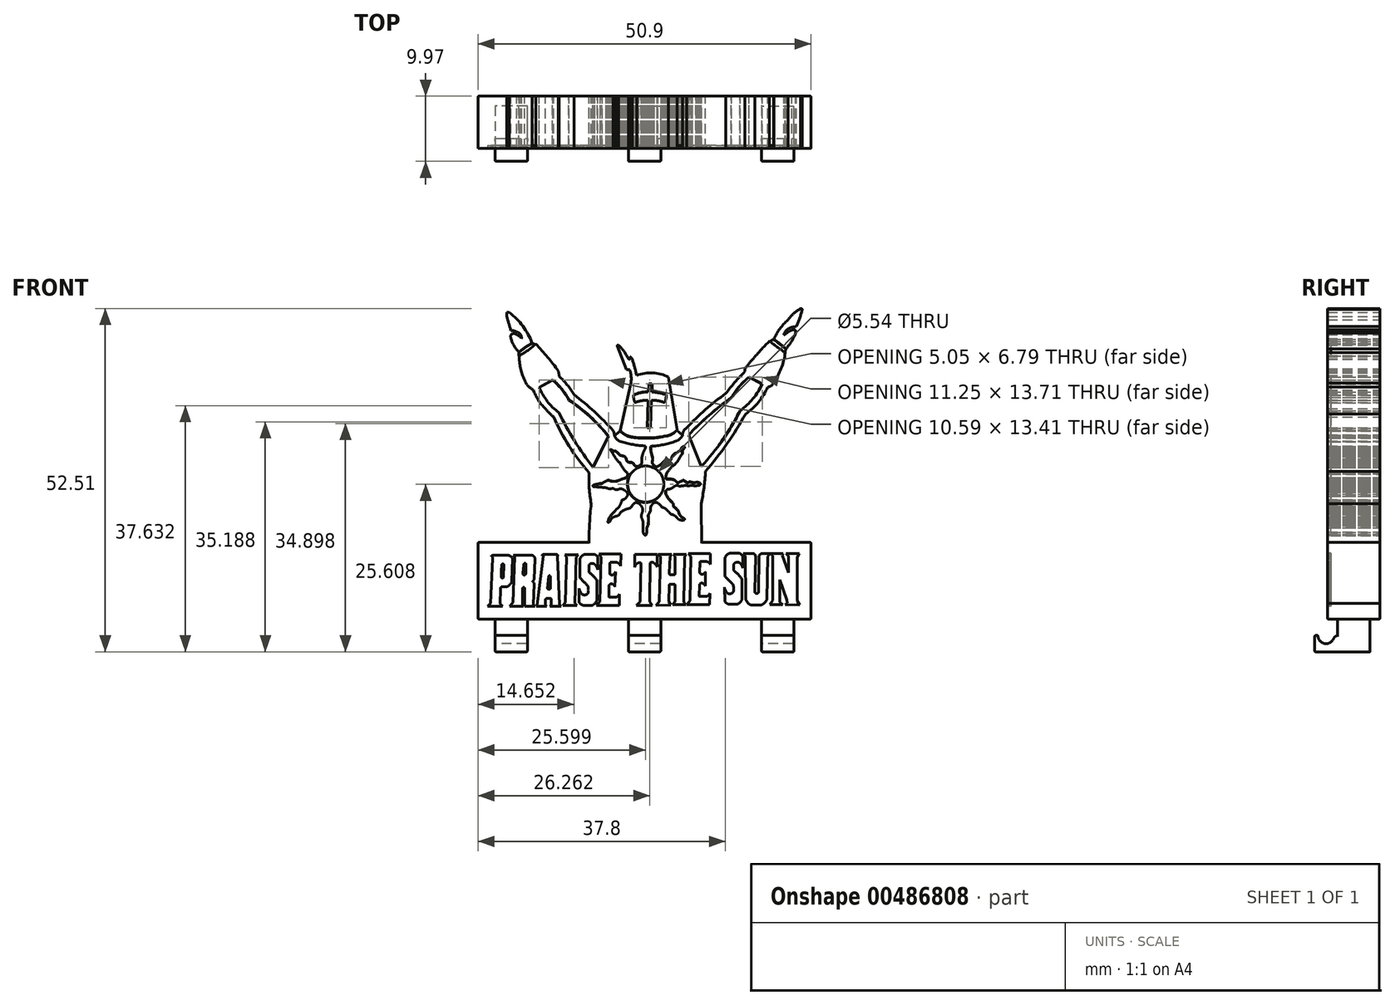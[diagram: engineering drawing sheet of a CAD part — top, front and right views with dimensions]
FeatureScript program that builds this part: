
annotation { "Feature Type Name" : "Feature", "Feature Type Description" : "" }
export const myFeature = defineFeature(function(context is Context, id is Id, definition is map)
    precondition{}
    {
        {
            var Q0;
            Q0=qCreatedBy(makeId("Front.planeOp"),FACE);
            var sketch = newSketch(context, id + "F0", { "sketchPlane" : qUnion([Q0])});
            skArc(sketch, "E0", {"start": v(-17.35, 21.56) * mm, "mid": v(-18.77, 24.15) * mm, "end": v(-20.84, 26.27) * mm});
            skLineSegment(sketch, "E1", {"start": v(-20.84, 26.27) * mm, "end": v(-21.25, 26.27) * mm});
            skLineSegment(sketch, "E2", {"start": v(-21.25, 26.27) * mm, "end": v(-21.25, 25.65) * mm});
            skArc(sketch, "E3", {"start": v(-21.25, 25.65) * mm, "mid": v(-20.93, 24.57) * mm, "end": v(-20.6, 23.5) * mm});
            skArc(sketch, "E4", {"start": v(-19.13, 22.87) * mm, "mid": v(-19.8, 23.33) * mm, "end": v(-20.6, 23.5) * mm});
            skArc(sketch, "E5", {"start": v(-18.99, 22.28) * mm, "mid": v(-19, 22.59) * mm, "end": v(-19.13, 22.87) * mm});
            skArc(sketch, "E6", {"start": v(-18.99, 22.28) * mm, "mid": v(-19.33, 22.61) * mm, "end": v(-19.74, 22.87) * mm});
            skArc(sketch, "E7", {"start": v(-19.74, 22.87) * mm, "mid": v(-20.17, 23.01) * mm, "end": v(-20.6, 22.87) * mm});
            skArc(sketch, "E8", {"start": v(-20.6, 22.87) * mm, "mid": v(-20.64, 22.57) * mm, "end": v(-20.6, 22.28) * mm});
            skArc(sketch, "E9", {"start": v(-20.6, 22.28) * mm, "mid": v(-20.1, 21.15) * mm, "end": v(-19.34, 20.18) * mm});
            skLineSegment(sketch, "E10", {"start": v(-17.35, 21.56) * mm, "end": v(-16.8, 21.42) * mm});
            skLineSegment(sketch, "E11", {"start": v(-19.34, 20.18) * mm, "end": v(-19.34, 19.66) * mm});
            skArc(sketch, "E12", {"start": v(-19.34, 19.66) * mm, "mid": v(-19.14, 17.75) * mm, "end": v(-18.52, 15.93) * mm});
            skArc(sketch, "E13", {"start": v(-18.52, 15.93) * mm, "mid": v(-18, 15.05) * mm, "end": v(-17.18, 14.43) * mm});
            skArc(sketch, "E14", {"start": v(-13.38, 17.3) * mm, "mid": v(-15, 19.43) * mm, "end": v(-16.8, 21.42) * mm});
            skArc(sketch, "E15", {"start": v(-13.25, 16.5) * mm, "mid": v(-13.28, 16.9) * mm, "end": v(-13.38, 17.3) * mm});
            skArc(sketch, "E16", {"start": v(-17.18, 14.43) * mm, "mid": v(-16.44, 12.88) * mm, "end": v(-15.37, 11.55) * mm});
            skArc(sketch, "E17", {"start": v(-10.97, 13.68) * mm, "mid": v(-12, 15.18) * mm, "end": v(-13.25, 16.5) * mm});
            skArc(sketch, "E18", {"start": v(-15.37, 11.55) * mm, "mid": v(-14.74, 10.88) * mm, "end": v(-14.07, 10.25) * mm});
            skArc(sketch, "E19", {"start": v(-14.07, 10.25) * mm, "mid": v(-11.7, 5.8) * mm, "end": v(-8.67, 1.79) * mm});
            skArc(sketch, "E20", {"start": v(-4.98, 8.2) * mm, "mid": v(-7.86, 11.08) * mm, "end": v(-10.97, 13.68) * mm});
            skArc(sketch, "E21", {"start": v(-4.77, 7.4) * mm, "mid": v(-4.84, 7.81) * mm, "end": v(-4.98, 8.2) * mm});
            skArc(sketch, "E22", {"start": v(-4.77, 7.4) * mm, "mid": v(-4.4, 6.86) * mm, "end": v(-3.88, 6.5) * mm});
            skArc(sketch, "E23", {"start": v(-3.88, 6.5) * mm, "mid": v(-1.96, 6.06) * mm, "end": v(0, 5.82) * mm});
            skArc(sketch, "E24", {"start": v(-8.67, 1.79) * mm, "mid": v(-8.64, -0.62) * mm, "end": v(-8.33, -3) * mm});
            skArc(sketch, "E25", {"start": v(-8.33, -3) * mm, "mid": v(-8.58, -5.96) * mm, "end": v(-8.67, -8.91) * mm});
            skLineSegment(sketch, "E26", {"start": v(-8.67, -8.91) * mm, "end": v(-24.71, -8.91) * mm});
            skLineSegment(sketch, "E27", {"start": v(-19.4, -10.71) * mm, "end": v(-19.4, -8.91) * mm, "construction": true});
            skLineSegment(sketch, "E28", {"start": v(-25.63, -18.85) * mm, "end": v(-25.63, -8.91) * mm});
            skLineSegment(sketch, "E29", {"start": v(-25.63, -8.91) * mm, "end": v(-24.71, -8.91) * mm});
            skLineSegment(sketch, "E30", {"start": v(-25.63, -18.85) * mm, "end": v(-25.63, -20.65) * mm, "construction": true});
            skLineSegment(sketch, "E31", {"start": v(-25.63, -20.65) * mm, "end": v(25.27, -20.65) * mm});
            skLineSegment(sketch, "E32", {"start": v(23.64, -18.26) * mm, "end": v(25.24, -18.26) * mm, "construction": true});
            skLineSegment(sketch, "E33", {"start": v(8.52, -8.91) * mm, "end": v(25.24, -8.91) * mm});
            skLineSegment(sketch, "E34", {"start": v(25.24, -8.91) * mm, "end": v(25.24, -18.26) * mm});
            skArc(sketch, "E35", {"start": v(8.52, -8.91) * mm, "mid": v(8.5, -5.96) * mm, "end": v(8.46, -3.01) * mm});
            skArc(sketch, "E36", {"start": v(8.46, -3.01) * mm, "mid": v(8.9, -0.54) * mm, "end": v(9.12, 1.96) * mm});
            skArc(sketch, "E37", {"start": v(9.12, 1.96) * mm, "mid": v(12.42, 6.18) * mm, "end": v(15.24, 10.73) * mm});
            skArc(sketch, "E38", {"start": v(15.24, 10.73) * mm, "mid": v(17.24, 12.54) * mm, "end": v(18.63, 14.86) * mm});
            skArc(sketch, "E39", {"start": v(18.63, 14.86) * mm, "mid": v(19.16, 15.03) * mm, "end": v(19.48, 15.48) * mm});
            skArc(sketch, "E40", {"start": v(19.48, 15.48) * mm, "mid": v(20.68, 17.68) * mm, "end": v(21.32, 20.1) * mm});
            skArc(sketch, "E41", {"start": v(21.42, 20.7) * mm, "mid": v(22.27, 21.81) * mm, "end": v(22.87, 23.07) * mm});
            skLineSegment(sketch, "E42", {"start": v(21.42, 20.7) * mm, "end": v(21.32, 20.1) * mm});
            skArc(sketch, "E43", {"start": v(22.87, 23.07) * mm, "mid": v(22.92, 23.31) * mm, "end": v(22.87, 23.55) * mm});
            skArc(sketch, "E44", {"start": v(22.87, 23.55) * mm, "mid": v(22.6, 23.61) * mm, "end": v(22.33, 23.55) * mm});
            skArc(sketch, "E45", {"start": v(22.33, 23.55) * mm, "mid": v(21.74, 23.26) * mm, "end": v(21.24, 22.84) * mm});
            skArc(sketch, "E46", {"start": v(21.11, 22.92) * mm, "mid": v(21.16, 22.85) * mm, "end": v(21.24, 22.84) * mm});
            skArc(sketch, "E47", {"start": v(22.16, 23.94) * mm, "mid": v(21.51, 23.56) * mm, "end": v(21.11, 22.92) * mm});
            skArc(sketch, "E48", {"start": v(23, 24.1) * mm, "mid": v(22.58, 24.04) * mm, "end": v(22.16, 23.94) * mm});
            skArc(sketch, "E49", {"start": v(23, 24.1) * mm, "mid": v(23.53, 25.38) * mm, "end": v(23.9, 26.72) * mm});
            skArc(sketch, "E50", {"start": v(23.9, 26.72) * mm, "mid": v(23.8, 26.84) * mm, "end": v(23.64, 26.85) * mm});
            skArc(sketch, "E51", {"start": v(23.64, 26.85) * mm, "mid": v(22.6, 26.08) * mm, "end": v(21.74, 25.12) * mm});
            skArc(sketch, "E52", {"start": v(21.74, 25.12) * mm, "mid": v(20.5, 23.76) * mm, "end": v(19.57, 22.17) * mm});
            skArc(sketch, "E53", {"start": v(18.92, 21.86) * mm, "mid": v(17.77, 20.71) * mm, "end": v(16.7, 19.49) * mm});
            skLineSegment(sketch, "E54", {"start": v(18.92, 21.86) * mm, "end": v(19.57, 22.17) * mm});
            skArc(sketch, "E55", {"start": v(16.7, 19.49) * mm, "mid": v(15.9, 18.58) * mm, "end": v(15.17, 17.62) * mm});
            skArc(sketch, "E56", {"start": v(15.17, 17.62) * mm, "mid": v(15.12, 17.42) * mm, "end": v(15.17, 17.22) * mm});
            skArc(sketch, "E57", {"start": v(15.17, 17.22) * mm, "mid": v(13.64, 15.6) * mm, "end": v(12.24, 13.86) * mm});
            skArc(sketch, "E58", {"start": v(12.24, 13.86) * mm, "mid": v(9.11, 11.38) * mm, "end": v(6.25, 8.6) * mm});
            skArc(sketch, "E59", {"start": v(6.25, 8.6) * mm, "mid": v(5.8, 8.15) * mm, "end": v(5.64, 7.54) * mm});
            skArc(sketch, "E60", {"start": v(4.62, 6.59) * mm, "mid": v(5.24, 6.95) * mm, "end": v(5.64, 7.54) * mm});
            skArc(sketch, "E61", {"start": v(0.76, 5.77) * mm, "mid": v(2.72, 6.04) * mm, "end": v(4.62, 6.59) * mm});
            skLineSegment(sketch, "E62", {"start": v(-4.77, 7.4) * mm, "end": v(-3.88, 8.17) * mm});
            skLineSegment(sketch, "E63", {"start": v(5.64, 7.54) * mm, "end": v(4.77, 8.3) * mm});
            skLineSegment(sketch, "E64", {"start": v(-3.88, 8.17) * mm, "end": v(-2.3, 15.25) * mm});
            skArc(sketch, "E65", {"start": v(-2.3, 15.25) * mm, "mid": v(-2.22, 16.4) * mm, "end": v(-2.47, 17.52) * mm});
            skLineSegment(sketch, "E66", {"start": v(-2.47, 17.52) * mm, "end": v(-2.97, 17.52) * mm});
            skLineSegment(sketch, "E67", {"start": v(-2.97, 17.52) * mm, "end": v(-4.36, 21.12) * mm});
            skArc(sketch, "E68", {"start": v(-4.31, 21.26) * mm, "mid": v(-4.36, 21.2) * mm, "end": v(-4.36, 21.12) * mm});
            skArc(sketch, "E69", {"start": v(-4.18, 21.26) * mm, "mid": v(-4.24, 21.28) * mm, "end": v(-4.31, 21.26) * mm});
            skArc(sketch, "E70", {"start": v(-2.66, 19.18) * mm, "mid": v(-3.32, 20.28) * mm, "end": v(-4.18, 21.26) * mm});
            skArc(sketch, "E71", {"start": v(-2.66, 19.18) * mm, "mid": v(-2.52, 19.11) * mm, "end": v(-2.39, 19.18) * mm});
            skArc(sketch, "E72", {"start": v(-2.39, 19.5) * mm, "mid": v(-2.41, 19.33) * mm, "end": v(-2.39, 19.18) * mm});
            skArc(sketch, "E73", {"start": v(-2.07, 19.13) * mm, "mid": v(-2.2, 19.33) * mm, "end": v(-2.39, 19.5) * mm});
            skArc(sketch, "E74", {"start": v(-1.4, 16.64) * mm, "mid": v(-1.7, 17.89) * mm, "end": v(-2.07, 19.13) * mm});
            skArc(sketch, "E75", {"start": v(3.5, 16.39) * mm, "mid": v(1.07, 17) * mm, "end": v(-1.4, 16.64) * mm});
            skLineSegment(sketch, "E76", {"start": v(3.5, 16.39) * mm, "end": v(4.77, 8.3) * mm});
            skCircle(sketch, "E77", {"center": v(0, 0) * mm, "radius": 2.77 * mm});
            skArc(sketch, "E78", {"start": v(-1.42, 2.69) * mm, "mid": v(-0.96, 2.83) * mm, "end": v(-0.6, 3.15) * mm});
            skArc(sketch, "E79", {"start": v(-1.84, 3.1) * mm, "mid": v(-1.66, 2.86) * mm, "end": v(-1.42, 2.69) * mm});
            skArc(sketch, "E80", {"start": v(-1.84, 3.1) * mm, "mid": v(-2.08, 3.3) * mm, "end": v(-2.4, 3.35) * mm});
            skArc(sketch, "E81", {"start": v(-2.94, 3.73) * mm, "mid": v(-2.73, 3.45) * mm, "end": v(-2.4, 3.35) * mm});
            skArc(sketch, "E82", {"start": v(-2.94, 3.73) * mm, "mid": v(-3, 3.96) * mm, "end": v(-3.13, 4.16) * mm});
            skArc(sketch, "E83", {"start": v(-3.13, 4.16) * mm, "mid": v(-3.47, 4.33) * mm, "end": v(-3.84, 4.4) * mm});
            skArc(sketch, "E84", {"start": v(-3.84, 4.4) * mm, "mid": v(-4.2, 4.71) * mm, "end": v(-4.54, 5.03) * mm});
            skArc(sketch, "E85", {"start": v(-4.54, 5.03) * mm, "mid": v(-4.74, 5.09) * mm, "end": v(-4.93, 5.03) * mm});
            skArc(sketch, "E86", {"start": v(-4.93, 5.03) * mm, "mid": v(-5.1, 5.2) * mm, "end": v(-5.34, 5.29) * mm});
            skArc(sketch, "E87", {"start": v(-5.34, 5.29) * mm, "mid": v(-5.39, 5.3) * mm, "end": v(-5.43, 5.27) * mm});
            skArc(sketch, "E88", {"start": v(-4.87, 4.36) * mm, "mid": v(-5.13, 4.83) * mm, "end": v(-5.43, 5.27) * mm});
            skArc(sketch, "E89", {"start": v(-4.87, 4.36) * mm, "mid": v(-4.4, 3.72) * mm, "end": v(-3.86, 3.14) * mm});
            skArc(sketch, "E90", {"start": v(-3.86, 3.14) * mm, "mid": v(-3.4, 2.35) * mm, "end": v(-2.79, 1.68) * mm});
            skArc(sketch, "E91", {"start": v(-2.97, 1) * mm, "mid": v(-2.8, 1.32) * mm, "end": v(-2.79, 1.68) * mm});
            skArc(sketch, "E92", {"start": v(-2.97, 1) * mm, "mid": v(-3.66, 0.78) * mm, "end": v(-4.33, 0.5) * mm});
            skArc(sketch, "E93", {"start": v(-5.33, 0.5) * mm, "mid": v(-4.83, 0.44) * mm, "end": v(-4.33, 0.5) * mm});
            skArc(sketch, "E94", {"start": v(-5.33, 0.5) * mm, "mid": v(-5.7, 0.6) * mm, "end": v(-6.05, 0.5) * mm});
            skArc(sketch, "E95", {"start": v(-6.05, 0.5) * mm, "mid": v(-6.37, 0.32) * mm, "end": v(-6.65, 0.12) * mm});
            skArc(sketch, "E96", {"start": v(-6.65, 0.12) * mm, "mid": v(-7.01, 0.1) * mm, "end": v(-7.36, 0) * mm});
            skArc(sketch, "E97", {"start": v(-7.36, 0) * mm, "mid": v(-7.57, 0) * mm, "end": v(-7.75, -0.1) * mm});
            skArc(sketch, "E98", {"start": v(-7.75, -0.1) * mm, "mid": v(-7.9, -0.11) * mm, "end": v(-8.04, -0.18) * mm});
            skArc(sketch, "E99", {"start": v(-8.04, -0.18) * mm, "mid": v(-8.06, -0.31) * mm, "end": v(-7.96, -0.4) * mm});
            skArc(sketch, "E100", {"start": v(-7.96, -0.4) * mm, "mid": v(-7.45, -0.43) * mm, "end": v(-6.93, -0.45) * mm});
            skArc(sketch, "E101", {"start": v(-6.93, -0.45) * mm, "mid": v(-6.45, -0.52) * mm, "end": v(-5.96, -0.57) * mm});
            skArc(sketch, "E102", {"start": v(-5.96, -0.57) * mm, "mid": v(-5.6, -0.71) * mm, "end": v(-5.2, -0.68) * mm});
            skArc(sketch, "E103", {"start": v(-4.92, -0.68) * mm, "mid": v(-5.06, -0.63) * mm, "end": v(-5.2, -0.68) * mm});
            skArc(sketch, "E104", {"start": v(-4.92, -0.68) * mm, "mid": v(-4.58, -0.86) * mm, "end": v(-4.2, -0.83) * mm});
            skArc(sketch, "E105", {"start": v(-3.54, -0.77) * mm, "mid": v(-3.88, -0.7) * mm, "end": v(-4.2, -0.83) * mm});
            skArc(sketch, "E106", {"start": v(-2.85, -1.23) * mm, "mid": v(-3.18, -0.98) * mm, "end": v(-3.54, -0.77) * mm});
            skArc(sketch, "E107", {"start": v(-2.85, -1.84) * mm, "mid": v(-2.74, -1.53) * mm, "end": v(-2.85, -1.23) * mm});
            skArc(sketch, "E108", {"start": v(-3.5, -2.4) * mm, "mid": v(-3.12, -2.18) * mm, "end": v(-2.85, -1.84) * mm});
            skArc(sketch, "E109", {"start": v(-3.5, -2.4) * mm, "mid": v(-3.65, -2.46) * mm, "end": v(-3.67, -2.62) * mm});
            skArc(sketch, "E110", {"start": v(-4.14, -3.6) * mm, "mid": v(-3.89, -3.12) * mm, "end": v(-3.67, -2.62) * mm});
            skArc(sketch, "E111", {"start": v(-4.14, -3.6) * mm, "mid": v(-4.5, -3.86) * mm, "end": v(-4.75, -4.2) * mm});
            skArc(sketch, "E112", {"start": v(-4.75, -4.2) * mm, "mid": v(-5.43, -4.91) * mm, "end": v(-5.81, -5.82) * mm});
            skArc(sketch, "E113", {"start": v(-5.81, -5.82) * mm, "mid": v(-5.63, -5.83) * mm, "end": v(-5.48, -5.72) * mm});
            skArc(sketch, "E114", {"start": v(-4.75, -4.96) * mm, "mid": v(-5.2, -5.26) * mm, "end": v(-5.48, -5.72) * mm});
            skArc(sketch, "E115", {"start": v(-4.75, -4.96) * mm, "mid": v(-4.37, -4.86) * mm, "end": v(-4.03, -4.67) * mm});
            skArc(sketch, "E116", {"start": v(-3.35, -3.99) * mm, "mid": v(-3.75, -4.27) * mm, "end": v(-4.03, -4.67) * mm});
            skArc(sketch, "E117", {"start": v(-2.4, -3.67) * mm, "mid": v(-2.88, -3.81) * mm, "end": v(-3.35, -3.99) * mm});
            skArc(sketch, "E118", {"start": v(-2.4, -3.67) * mm, "mid": v(-2.28, -3.6) * mm, "end": v(-2.21, -3.5) * mm});
            skArc(sketch, "E119", {"start": v(-1.6, -2.84) * mm, "mid": v(-1.95, -3.13) * mm, "end": v(-2.21, -3.5) * mm});
            skArc(sketch, "E120", {"start": v(-1.08, -2.94) * mm, "mid": v(-1.33, -2.85) * mm, "end": v(-1.6, -2.84) * mm});
            skArc(sketch, "E121", {"start": v(-0.53, -3.6) * mm, "mid": v(-0.77, -3.24) * mm, "end": v(-1.08, -2.94) * mm});
            skArc(sketch, "E122", {"start": v(-0.58, -4.46) * mm, "mid": v(-0.49, -4.03) * mm, "end": v(-0.53, -3.6) * mm});
            skArc(sketch, "E123", {"start": v(-0.58, -4.46) * mm, "mid": v(-0.67, -4.8) * mm, "end": v(-0.64, -5.16) * mm});
            skArc(sketch, "E124", {"start": v(-0.39, -5.95) * mm, "mid": v(-0.48, -5.54) * mm, "end": v(-0.64, -5.16) * mm});
            skArc(sketch, "E125", {"start": v(-0.39, -7.32) * mm, "mid": v(-0.38, -6.63) * mm, "end": v(-0.39, -5.95) * mm});
            skArc(sketch, "E126", {"start": v(-0.39, -7.32) * mm, "mid": v(-0.31, -7.6) * mm, "end": v(-0.12, -7.82) * mm});
            skArc(sketch, "E127", {"start": v(-0.12, -7.82) * mm, "mid": v(0.02, -7.78) * mm, "end": v(0.1, -7.65) * mm});
            skArc(sketch, "E128", {"start": v(0.1, -7.65) * mm, "mid": v(0.18, -7.16) * mm, "end": v(0.19, -6.66) * mm});
            skArc(sketch, "E129", {"start": v(0.19, -6.66) * mm, "mid": v(0.26, -6.52) * mm, "end": v(0.28, -6.36) * mm});
            skArc(sketch, "E130", {"start": v(0.28, -6.36) * mm, "mid": v(0.37, -6.26) * mm, "end": v(0.4, -6.12) * mm});
            skArc(sketch, "E131", {"start": v(0.4, -6.12) * mm, "mid": v(0.42, -5.4) * mm, "end": v(0.4, -4.67) * mm});
            skArc(sketch, "E132", {"start": v(0.4, -4.67) * mm, "mid": v(0.49, -4.58) * mm, "end": v(0.54, -4.46) * mm});
            skArc(sketch, "E133", {"start": v(0.54, -4.46) * mm, "mid": v(0.62, -4.34) * mm, "end": v(0.65, -4.2) * mm});
            skArc(sketch, "E134", {"start": v(0.65, -4.2) * mm, "mid": v(0.75, -4.03) * mm, "end": v(0.75, -3.83) * mm});
            skArc(sketch, "E135", {"start": v(0.85, -3.32) * mm, "mid": v(0.76, -3.57) * mm, "end": v(0.75, -3.83) * mm});
            skArc(sketch, "E136", {"start": v(1.3, -2.84) * mm, "mid": v(1.04, -3.05) * mm, "end": v(0.85, -3.32) * mm});
            skArc(sketch, "E137", {"start": v(1.86, -2.9) * mm, "mid": v(1.58, -2.82) * mm, "end": v(1.3, -2.84) * mm});
            skArc(sketch, "E138", {"start": v(2.39, -3.42) * mm, "mid": v(2.15, -3.13) * mm, "end": v(1.86, -2.9) * mm});
            skArc(sketch, "E139", {"start": v(2.39, -3.42) * mm, "mid": v(2.5, -3.56) * mm, "end": v(2.69, -3.6) * mm});
            skArc(sketch, "E140", {"start": v(3.4, -4.14) * mm, "mid": v(3.08, -3.82) * mm, "end": v(2.69, -3.6) * mm});
            skArc(sketch, "E141", {"start": v(3.92, -4.67) * mm, "mid": v(3.66, -4.4) * mm, "end": v(3.4, -4.14) * mm});
            skArc(sketch, "E142", {"start": v(3.92, -4.67) * mm, "mid": v(4.03, -4.68) * mm, "end": v(4.14, -4.67) * mm});
            skArc(sketch, "E143", {"start": v(4.81, -5.21) * mm, "mid": v(4.51, -4.9) * mm, "end": v(4.14, -4.67) * mm});
            skArc(sketch, "E144", {"start": v(4.81, -5.21) * mm, "mid": v(5.02, -5.38) * mm, "end": v(5.26, -5.48) * mm});
            skArc(sketch, "E145", {"start": v(5.26, -5.48) * mm, "mid": v(5.6, -5.52) * mm, "end": v(5.94, -5.48) * mm});
            skArc(sketch, "E146", {"start": v(5.94, -5.48) * mm, "mid": v(5.93, -5.32) * mm, "end": v(5.8, -5.21) * mm});
            skArc(sketch, "E147", {"start": v(5.12, -4.53) * mm, "mid": v(5.41, -4.92) * mm, "end": v(5.8, -5.21) * mm});
            skArc(sketch, "E148", {"start": v(5.04, -4.2) * mm, "mid": v(5.08, -4.37) * mm, "end": v(5.12, -4.53) * mm});
            skArc(sketch, "E149", {"start": v(5.04, -4.2) * mm, "mid": v(4.7, -3.76) * mm, "end": v(4.26, -3.41) * mm});
            skArc(sketch, "E150", {"start": v(4.26, -3.41) * mm, "mid": v(4.23, -3.12) * mm, "end": v(4.14, -2.85) * mm});
            skArc(sketch, "E151", {"start": v(3.1, -1.55) * mm, "mid": v(3.55, -2.25) * mm, "end": v(4.14, -2.85) * mm});
            skArc(sketch, "E152", {"start": v(3.1, -0.98) * mm, "mid": v(3.06, -1.26) * mm, "end": v(3.1, -1.55) * mm});
            skArc(sketch, "E153", {"start": v(3.31, -0.77) * mm, "mid": v(3.2, -0.86) * mm, "end": v(3.1, -0.98) * mm});
            skArc(sketch, "E154", {"start": v(3.31, -0.77) * mm, "mid": v(3.57, -0.76) * mm, "end": v(3.83, -0.7) * mm});
            skArc(sketch, "E155", {"start": v(3.83, -0.7) * mm, "mid": v(4.14, -0.53) * mm, "end": v(4.42, -0.3) * mm});
            skArc(sketch, "E156", {"start": v(4.92, -0.21) * mm, "mid": v(4.66, -0.22) * mm, "end": v(4.42, -0.3) * mm});
            skArc(sketch, "E157", {"start": v(4.92, -0.21) * mm, "mid": v(5.13, -0.31) * mm, "end": v(5.36, -0.3) * mm});
            skArc(sketch, "E158", {"start": v(5.36, -0.3) * mm, "mid": v(5.69, -0.27) * mm, "end": v(6, -0.19) * mm});
            skArc(sketch, "E159", {"start": v(6.22, -0.21) * mm, "mid": v(6.12, -0.18) * mm, "end": v(6, -0.19) * mm});
            skArc(sketch, "E160", {"start": v(6.22, -0.21) * mm, "mid": v(6.43, -0.28) * mm, "end": v(6.66, -0.27) * mm});
            skArc(sketch, "E161", {"start": v(7.11, -0.19) * mm, "mid": v(6.88, -0.2) * mm, "end": v(6.66, -0.27) * mm});
            skArc(sketch, "E162", {"start": v(7.11, -0.19) * mm, "mid": v(7.52, -0.26) * mm, "end": v(7.93, -0.21) * mm});
            skArc(sketch, "E163", {"start": v(8.2, -0.19) * mm, "mid": v(8.07, -0.18) * mm, "end": v(7.93, -0.21) * mm});
            skArc(sketch, "E164", {"start": v(8.2, -0.19) * mm, "mid": v(8.28, -0.14) * mm, "end": v(8.32, -0.06) * mm});
            skArc(sketch, "E165", {"start": v(8.32, -0.06) * mm, "mid": v(8.38, -0.03) * mm, "end": v(8.4, 0.03) * mm});
            skArc(sketch, "E166", {"start": v(8.4, 0.03) * mm, "mid": v(8.37, 0.08) * mm, "end": v(8.32, 0.13) * mm});
            skArc(sketch, "E167", {"start": v(8.32, 0.13) * mm, "mid": v(8.27, 0.2) * mm, "end": v(8.2, 0.24) * mm});
            skArc(sketch, "E168", {"start": v(8.2, 0.24) * mm, "mid": v(8.12, 0.24) * mm, "end": v(8.04, 0.24) * mm});
            skArc(sketch, "E169", {"start": v(8.04, 0.24) * mm, "mid": v(8, 0.29) * mm, "end": v(7.93, 0.32) * mm});
            skArc(sketch, "E170", {"start": v(7.93, 0.32) * mm, "mid": v(7.81, 0.32) * mm, "end": v(7.7, 0.29) * mm});
            skArc(sketch, "E171", {"start": v(7.17, 0.2) * mm, "mid": v(7.44, 0.23) * mm, "end": v(7.7, 0.29) * mm});
            skArc(sketch, "E172", {"start": v(7.17, 0.2) * mm, "mid": v(7.07, 0.3) * mm, "end": v(6.94, 0.32) * mm});
            skArc(sketch, "E173", {"start": v(6.94, 0.32) * mm, "mid": v(6.77, 0.36) * mm, "end": v(6.6, 0.32) * mm});
            skArc(sketch, "E174", {"start": v(6.37, 0.24) * mm, "mid": v(6.5, 0.25) * mm, "end": v(6.6, 0.32) * mm});
            skArc(sketch, "E175", {"start": v(6.37, 0.24) * mm, "mid": v(6.27, 0.32) * mm, "end": v(6.15, 0.37) * mm});
            skArc(sketch, "E176", {"start": v(6.15, 0.37) * mm, "mid": v(6.04, 0.44) * mm, "end": v(5.92, 0.49) * mm});
            skArc(sketch, "E177", {"start": v(5.92, 0.49) * mm, "mid": v(5.85, 0.57) * mm, "end": v(5.75, 0.6) * mm});
            skArc(sketch, "E178", {"start": v(5.75, 0.6) * mm, "mid": v(5.64, 0.56) * mm, "end": v(5.56, 0.49) * mm});
            skArc(sketch, "E179", {"start": v(5.56, 0.49) * mm, "mid": v(5.44, 0.47) * mm, "end": v(5.33, 0.4) * mm});
            skArc(sketch, "E180", {"start": v(5.33, 0.4) * mm, "mid": v(5.21, 0.36) * mm, "end": v(5.12, 0.29) * mm});
            skArc(sketch, "E181", {"start": v(4.96, 0.24) * mm, "mid": v(5.04, 0.25) * mm, "end": v(5.12, 0.29) * mm});
            skArc(sketch, "E182", {"start": v(4.76, 0.32) * mm, "mid": v(4.85, 0.26) * mm, "end": v(4.96, 0.24) * mm});
            skArc(sketch, "E183", {"start": v(4.36, 0.68) * mm, "mid": v(4.56, 0.5) * mm, "end": v(4.76, 0.32) * mm});
            skArc(sketch, "E184", {"start": v(4.36, 0.68) * mm, "mid": v(3.82, 0.79) * mm, "end": v(3.28, 0.8) * mm});
            skArc(sketch, "E185", {"start": v(3.1, 1.02) * mm, "mid": v(3.13, 0.87) * mm, "end": v(3.28, 0.8) * mm});
            skArc(sketch, "E186", {"start": v(3.17, 1.57) * mm, "mid": v(3.11, 1.3) * mm, "end": v(3.1, 1.02) * mm});
            skArc(sketch, "E187", {"start": v(4.4, 3) * mm, "mid": v(3.71, 2.35) * mm, "end": v(3.17, 1.57) * mm});
            skArc(sketch, "E188", {"start": v(4.4, 3) * mm, "mid": v(4.8, 3.42) * mm, "end": v(5.12, 3.93) * mm});
            skArc(sketch, "E189", {"start": v(5.6, 4.62) * mm, "mid": v(5.33, 4.3) * mm, "end": v(5.12, 3.93) * mm});
            skArc(sketch, "E190", {"start": v(5.6, 4.62) * mm, "mid": v(5.61, 4.86) * mm, "end": v(5.6, 5.1) * mm});
            skArc(sketch, "E191", {"start": v(5.92, 5.5) * mm, "mid": v(5.75, 5.3) * mm, "end": v(5.6, 5.1) * mm});
            skArc(sketch, "E192", {"start": v(5.92, 5.5) * mm, "mid": v(5.95, 5.62) * mm, "end": v(5.92, 5.73) * mm});
            skArc(sketch, "E193", {"start": v(5.92, 5.73) * mm, "mid": v(5.8, 5.74) * mm, "end": v(5.68, 5.73) * mm});
            skArc(sketch, "E194", {"start": v(5.68, 5.73) * mm, "mid": v(5.44, 5.5) * mm, "end": v(5.33, 5.2) * mm});
            skArc(sketch, "E195", {"start": v(5.33, 5.2) * mm, "mid": v(5, 5) * mm, "end": v(4.7, 4.76) * mm});
            skArc(sketch, "E196", {"start": v(4.7, 4.76) * mm, "mid": v(4.44, 4.68) * mm, "end": v(4.22, 4.52) * mm});
            skArc(sketch, "E197", {"start": v(4.22, 4.52) * mm, "mid": v(4.01, 4.22) * mm, "end": v(3.93, 3.86) * mm});
            skArc(sketch, "E198", {"start": v(3.67, 3.63) * mm, "mid": v(3.83, 3.7) * mm, "end": v(3.93, 3.86) * mm});
            skArc(sketch, "E199", {"start": v(3.67, 3.63) * mm, "mid": v(3.26, 3.63) * mm, "end": v(2.86, 3.58) * mm});
            skArc(sketch, "E200", {"start": v(2.86, 3.58) * mm, "mid": v(2.75, 3.5) * mm, "end": v(2.66, 3.4) * mm});
            skArc(sketch, "E201", {"start": v(1.76, 2.68) * mm, "mid": v(2.25, 3) * mm, "end": v(2.66, 3.4) * mm});
            skArc(sketch, "E202", {"start": v(1.31, 2.83) * mm, "mid": v(1.52, 2.69) * mm, "end": v(1.76, 2.68) * mm});
            skArc(sketch, "E203", {"start": v(0.98, 3.3) * mm, "mid": v(1.13, 3.05) * mm, "end": v(1.31, 2.83) * mm});
            skArc(sketch, "E204", {"start": v(0.98, 3.3) * mm, "mid": v(1.04, 3.59) * mm, "end": v(1.07, 3.88) * mm});
            skArc(sketch, "E205", {"start": v(1.07, 3.88) * mm, "mid": v(1.02, 4.23) * mm, "end": v(0.91, 4.57) * mm});
            skArc(sketch, "E206", {"start": v(0.76, 5.77) * mm, "mid": v(0.8, 5.17) * mm, "end": v(0.91, 4.57) * mm});
            skArc(sketch, "E207", {"start": v(-0.19, 5.23) * mm, "mid": v(-0.05, 5.51) * mm, "end": v(0, 5.82) * mm});
            skArc(sketch, "E208", {"start": v(-0.19, 5.23) * mm, "mid": v(-0.37, 4.86) * mm, "end": v(-0.49, 4.46) * mm});
            skArc(sketch, "E209", {"start": v(-0.49, 4.46) * mm, "mid": v(-0.62, 3.81) * mm, "end": v(-0.6, 3.15) * mm});
            skLineSegment(sketch, "E210", {"start": v(0.33, 12.82) * mm, "end": v(0.23, 8.6) * mm});
            skLineSegment(sketch, "E211", {"start": v(0.23, 8.6) * mm, "end": v(0.73, 8.59) * mm});
            skLineSegment(sketch, "E212", {"start": v(0.73, 8.59) * mm, "end": v(0.89, 12.84) * mm});
            skArc(sketch, "E213", {"start": v(0.33, 12.82) * mm, "mid": v(-0.68, 12.75) * mm, "end": v(-1.66, 12.48) * mm});
            skArc(sketch, "E214", {"start": v(2.87, 12.47) * mm, "mid": v(1.9, 12.74) * mm, "end": v(0.89, 12.84) * mm});
            skArc(sketch, "E215", {"start": v(-1.9, 13.62) * mm, "mid": v(-1.82, 13.04) * mm, "end": v(-1.66, 12.48) * mm});
            skArc(sketch, "E216", {"start": v(0.33, 14.12) * mm, "mid": v(-0.8, 14) * mm, "end": v(-1.9, 13.62) * mm});
            skArc(sketch, "E217", {"start": v(2.87, 12.47) * mm, "mid": v(3.1, 13.07) * mm, "end": v(3.16, 13.7) * mm});
            skArc(sketch, "E218", {"start": v(3.16, 13.7) * mm, "mid": v(2.07, 14) * mm, "end": v(0.95, 14.12) * mm});
            skArc(sketch, "E219", {"start": v(0.33, 14.12) * mm, "mid": v(0.46, 14.72) * mm, "end": v(0.5, 15.32) * mm});
            skArc(sketch, "E220", {"start": v(0.95, 14.12) * mm, "mid": v(0.97, 14.72) * mm, "end": v(0.95, 15.32) * mm});
            skArc(sketch, "E221", {"start": v(0.95, 15.32) * mm, "mid": v(0.73, 15.38) * mm, "end": v(0.5, 15.32) * mm});
            skArc(sketch, "E222", {"start": v(13.11, 13.27) * mm, "mid": v(9.69, 10.54) * mm, "end": v(6.54, 7.49) * mm});
            skArc(sketch, "E223", {"start": v(15.8, 16.4) * mm, "mid": v(14.32, 14.95) * mm, "end": v(13.11, 13.27) * mm});
            skArc(sketch, "E224", {"start": v(8.49, 2.68) * mm, "mid": v(11.75, 6.76) * mm, "end": v(14.43, 11.24) * mm});
            skArc(sketch, "E225", {"start": v(14.43, 11.24) * mm, "mid": v(16.38, 13.05) * mm, "end": v(17.8, 15.32) * mm});
            skLineSegment(sketch, "E226", {"start": v(6.54, 7.49) * mm, "end": v(8.49, 2.68) * mm});
            skLineSegment(sketch, "E227", {"start": v(17.8, 15.32) * mm, "end": v(15.8, 16.4) * mm});
            skArc(sketch, "E228", {"start": v(-16.27, 14.8) * mm, "mid": v(-15.05, 12.67) * mm, "end": v(-13.28, 10.95) * mm});
            skArc(sketch, "E229", {"start": v(-11.72, 12.88) * mm, "mid": v(-12.81, 14.54) * mm, "end": v(-14.2, 15.95) * mm});
            skArc(sketch, "E230", {"start": v(-13.28, 10.95) * mm, "mid": v(-10.87, 6.62) * mm, "end": v(-8.06, 2.54) * mm});
            skArc(sketch, "E231", {"start": v(-5.68, 7.35) * mm, "mid": v(-8.5, 10.34) * mm, "end": v(-11.72, 12.88) * mm});
            skLineSegment(sketch, "E232", {"start": v(-16.27, 14.8) * mm, "end": v(-14.2, 15.95) * mm});
            skLineSegment(sketch, "E233", {"start": v(-8.06, 2.54) * mm, "end": v(-5.68, 7.35) * mm});
            skLineSegment(sketch, "E234", {"start": v(25.24, -18.26) * mm, "end": v(25.27, -20.65) * mm});
            skLineSegment(sketch, "E235", {"start": v(-25.63, -20.65) * mm, "end": v(-25.63, -18.85) * mm});
            skArc(sketch, "E236", {"start": v(-3.88, 8.17) * mm, "mid": v(-3.23, 7.64) * mm, "end": v(-2.46, 7.29) * mm});
            skArc(sketch, "E237", {"start": v(-2.46, 7.29) * mm, "mid": v(-1.24, 7.1) * mm, "end": v(0, 7.07) * mm});
            skArc(sketch, "E238", {"start": v(2.99, 7.37) * mm, "mid": v(3.98, 7.64) * mm, "end": v(4.77, 8.3) * mm});
            skArc(sketch, "E239", {"start": v(0, 7.07) * mm, "mid": v(1.5, 7.12) * mm, "end": v(2.99, 7.37) * mm});
            skArc(sketch, "E240", {"start": v(18.92, 21.86) * mm, "mid": v(20.1, 20.96) * mm, "end": v(21.32, 20.1) * mm});
            skArc(sketch, "E241", {"start": v(21.42, 20.7) * mm, "mid": v(20.5, 21.45) * mm, "end": v(19.57, 22.17) * mm});
            skArc(sketch, "E242", {"start": v(-17.35, 21.56) * mm, "mid": v(-18.39, 20.93) * mm, "end": v(-19.34, 20.18) * mm});
            skArc(sketch, "E243", {"start": v(-19.34, 19.66) * mm, "mid": v(-18.01, 20.46) * mm, "end": v(-16.8, 21.42) * mm});
            skSolve(sketch);
        }
        {
            var Q0;
            Q0=makeQuery(id+"F0.imprint","IMPRINT",FACE,{"disambiguationData":[TD([[makeQuery(id+"F0.imprint","IMPRINT",EDGE,{"derivedFrom":sQuery(id+"F0.wireOp",EDGE,"E12")}),1.0]])]});
            var Q1;
            Q1=makeQuery(id+"F0.imprint","IMPRINT",FACE,{"disambiguationData":[TD([[makeQuery(id+"F0.imprint","IMPRINT",EDGE,{"derivedFrom":sQuery(id+"F0.wireOp",EDGE,"E0")}),1.0]])]});
            var Q2;
            Q2=makeQuery(id+"F0.imprint","IMPRINT",FACE,{"disambiguationData":[TD([[makeQuery(id+"F0.imprint","IMPRINT",EDGE,{"derivedFrom":sQuery(id+"F0.wireOp",EDGE,"E64")}),-1.0]])]});
            var Q3;
            Q3=makeQuery(id+"F0.imprint","IMPRINT",FACE,{"disambiguationData":[TD([[makeQuery(id+"F0.imprint","IMPRINT",EDGE,{"derivedFrom":sQuery(id+"F0.wireOp",EDGE,"E41")}),1.0]])]});
            var Q4;
            Q4=makeQuery(id+"F0.imprint","IMPRINT",FACE,{"disambiguationData":[TD([[makeQuery(id+"F0.imprint","IMPRINT",EDGE,{"derivedFrom":sQuery(id+"F0.wireOp",EDGE,"E77")}),1.0]])]});
            extrude(context, id + "F1", {"entities" : qUnion([Q0, Q1, Q2, Q3, Q4]), "depth" : 8 * mm});
        }
        {
            var Q0;
            Q0=qCreatedBy(makeId("Front.planeOp"),FACE);
            var sketch = newSketch(context, id + "F2", { "sketchPlane" : qUnion([Q0])});
            skArc(sketch, "E244", {"start": v(-17.38, 21.52) * mm, "mid": v(-18.8, 24.11) * mm, "end": v(-20.87, 26.23) * mm});
            skLineSegment(sketch, "E245", {"start": v(-20.87, 26.23) * mm, "end": v(-21.28, 26.23) * mm});
            skLineSegment(sketch, "E246", {"start": v(-21.28, 26.23) * mm, "end": v(-21.28, 25.6) * mm});
            skArc(sketch, "E247", {"start": v(-21.28, 25.6) * mm, "mid": v(-20.96, 24.53) * mm, "end": v(-20.63, 23.45) * mm});
            skArc(sketch, "E248", {"start": v(-19.16, 22.83) * mm, "mid": v(-19.83, 23.29) * mm, "end": v(-20.63, 23.45) * mm});
            skArc(sketch, "E249", {"start": v(-19.02, 22.24) * mm, "mid": v(-19.03, 22.55) * mm, "end": v(-19.16, 22.83) * mm});
            skArc(sketch, "E250", {"start": v(-19.02, 22.24) * mm, "mid": v(-19.36, 22.57) * mm, "end": v(-19.77, 22.83) * mm});
            skArc(sketch, "E251", {"start": v(-19.77, 22.83) * mm, "mid": v(-20.2, 22.97) * mm, "end": v(-20.63, 22.83) * mm});
            skArc(sketch, "E252", {"start": v(-20.63, 22.83) * mm, "mid": v(-20.67, 22.53) * mm, "end": v(-20.63, 22.24) * mm});
            skArc(sketch, "E253", {"start": v(-20.63, 22.24) * mm, "mid": v(-20.14, 21.1) * mm, "end": v(-19.38, 20.14) * mm});
            skLineSegment(sketch, "E254", {"start": v(-17.38, 21.52) * mm, "end": v(-16.83, 21.38) * mm});
            skLineSegment(sketch, "E255", {"start": v(-19.38, 20.14) * mm, "end": v(-19.38, 19.62) * mm});
            skArc(sketch, "E256", {"start": v(-19.38, 19.62) * mm, "mid": v(-19.17, 17.7) * mm, "end": v(-18.55, 15.89) * mm});
            skArc(sketch, "E257", {"start": v(-18.55, 15.89) * mm, "mid": v(-18.03, 15) * mm, "end": v(-17.2, 14.38) * mm});
            skArc(sketch, "E258", {"start": v(-13.4, 17.25) * mm, "mid": v(-15.03, 19.39) * mm, "end": v(-16.83, 21.38) * mm});
            skArc(sketch, "E259", {"start": v(-13.28, 16.46) * mm, "mid": v(-13.3, 16.86) * mm, "end": v(-13.4, 17.25) * mm});
            skArc(sketch, "E260", {"start": v(-17.2, 14.38) * mm, "mid": v(-16.47, 12.84) * mm, "end": v(-15.4, 11.5) * mm});
            skArc(sketch, "E261", {"start": v(-11, 13.64) * mm, "mid": v(-12.03, 15.14) * mm, "end": v(-13.28, 16.46) * mm});
            skArc(sketch, "E262", {"start": v(-15.4, 11.5) * mm, "mid": v(-14.77, 10.84) * mm, "end": v(-14.1, 10.2) * mm});
            skArc(sketch, "E263", {"start": v(-14.1, 10.2) * mm, "mid": v(-11.73, 5.77) * mm, "end": v(-8.7, 1.75) * mm});
            skArc(sketch, "E264", {"start": v(-5.02, 8.16) * mm, "mid": v(-7.89, 11.04) * mm, "end": v(-11, 13.64) * mm});
            skArc(sketch, "E265", {"start": v(-4.8, 7.35) * mm, "mid": v(-4.87, 7.77) * mm, "end": v(-5.02, 8.16) * mm});
            skArc(sketch, "E266", {"start": v(-4.8, 7.35) * mm, "mid": v(-4.44, 6.82) * mm, "end": v(-3.9, 6.46) * mm});
            skArc(sketch, "E267", {"start": v(-3.9, 6.46) * mm, "mid": v(-1.99, 6.02) * mm, "end": v(-0.03, 5.78) * mm});
            skArc(sketch, "E268", {"start": v(-8.7, 1.75) * mm, "mid": v(-8.67, -0.66) * mm, "end": v(-8.36, -3.05) * mm});
            skArc(sketch, "E269", {"start": v(-8.36, -3.05) * mm, "mid": v(-8.61, -6) * mm, "end": v(-8.7, -8.96) * mm});
            skLineSegment(sketch, "E270", {"start": v(-8.7, -8.96) * mm, "end": v(-24.75, -8.96) * mm});
            skLineSegment(sketch, "E271", {"start": v(-19.44, -10.76) * mm, "end": v(-19.44, -8.96) * mm, "construction": true});
            skLineSegment(sketch, "E272", {"start": v(-25.66, -18.9) * mm, "end": v(-25.66, -8.96) * mm});
            skLineSegment(sketch, "E273", {"start": v(-25.66, -8.96) * mm, "end": v(-24.75, -8.96) * mm});
            skLineSegment(sketch, "E274", {"start": v(-25.66, -18.9) * mm, "end": v(-25.66, -20.7) * mm, "construction": true});
            skLineSegment(sketch, "E275", {"start": v(-25.66, -20.7) * mm, "end": v(25.24, -20.7) * mm});
            skLineSegment(sketch, "E276", {"start": v(23.6, -18.3) * mm, "end": v(25.2, -18.3) * mm, "construction": true});
            skLineSegment(sketch, "E277", {"start": v(8.48, -8.96) * mm, "end": v(25.2, -8.96) * mm});
            skLineSegment(sketch, "E278", {"start": v(25.2, -8.96) * mm, "end": v(25.2, -18.3) * mm});
            skArc(sketch, "E279", {"start": v(8.48, -8.96) * mm, "mid": v(8.48, -6) * mm, "end": v(8.43, -3.06) * mm});
            skArc(sketch, "E280", {"start": v(8.43, -3.06) * mm, "mid": v(8.87, -0.58) * mm, "end": v(9.1, 1.91) * mm});
            skArc(sketch, "E281", {"start": v(9.1, 1.91) * mm, "mid": v(12.4, 6.13) * mm, "end": v(15.2, 10.69) * mm});
            skArc(sketch, "E282", {"start": v(15.2, 10.69) * mm, "mid": v(17.21, 12.5) * mm, "end": v(18.6, 14.82) * mm});
            skArc(sketch, "E283", {"start": v(18.6, 14.82) * mm, "mid": v(19.13, 15) * mm, "end": v(19.45, 15.44) * mm});
            skArc(sketch, "E284", {"start": v(19.45, 15.44) * mm, "mid": v(20.65, 17.64) * mm, "end": v(21.29, 20.07) * mm});
            skArc(sketch, "E285", {"start": v(21.4, 20.66) * mm, "mid": v(22.24, 21.77) * mm, "end": v(22.84, 23.03) * mm});
            skLineSegment(sketch, "E286", {"start": v(21.4, 20.66) * mm, "end": v(21.29, 20.07) * mm});
            skArc(sketch, "E287", {"start": v(22.84, 23.03) * mm, "mid": v(22.9, 23.27) * mm, "end": v(22.84, 23.5) * mm});
            skArc(sketch, "E288", {"start": v(22.84, 23.5) * mm, "mid": v(22.57, 23.57) * mm, "end": v(22.3, 23.5) * mm});
            skArc(sketch, "E289", {"start": v(22.3, 23.5) * mm, "mid": v(21.71, 23.22) * mm, "end": v(21.21, 22.8) * mm});
            skArc(sketch, "E290", {"start": v(21.08, 22.88) * mm, "mid": v(21.13, 22.8) * mm, "end": v(21.21, 22.8) * mm});
            skArc(sketch, "E291", {"start": v(22.13, 23.9) * mm, "mid": v(21.48, 23.51) * mm, "end": v(21.08, 22.88) * mm});
            skArc(sketch, "E292", {"start": v(22.98, 24.05) * mm, "mid": v(22.55, 24) * mm, "end": v(22.13, 23.9) * mm});
            skArc(sketch, "E293", {"start": v(22.98, 24.05) * mm, "mid": v(23.5, 25.34) * mm, "end": v(23.88, 26.67) * mm});
            skArc(sketch, "E294", {"start": v(23.88, 26.67) * mm, "mid": v(23.77, 26.8) * mm, "end": v(23.61, 26.8) * mm});
            skArc(sketch, "E295", {"start": v(23.61, 26.8) * mm, "mid": v(22.57, 26.04) * mm, "end": v(21.7, 25.08) * mm});
            skArc(sketch, "E296", {"start": v(21.7, 25.08) * mm, "mid": v(20.46, 23.72) * mm, "end": v(19.54, 22.13) * mm});
            skArc(sketch, "E297", {"start": v(18.89, 21.82) * mm, "mid": v(17.74, 20.67) * mm, "end": v(16.67, 19.44) * mm});
            skLineSegment(sketch, "E298", {"start": v(18.89, 21.82) * mm, "end": v(19.54, 22.13) * mm});
            skArc(sketch, "E299", {"start": v(16.67, 19.44) * mm, "mid": v(15.87, 18.54) * mm, "end": v(15.14, 17.58) * mm});
            skArc(sketch, "E300", {"start": v(15.14, 17.58) * mm, "mid": v(15.1, 17.38) * mm, "end": v(15.14, 17.18) * mm});
            skArc(sketch, "E301", {"start": v(15.14, 17.18) * mm, "mid": v(13.6, 15.56) * mm, "end": v(12.21, 13.82) * mm});
            skArc(sketch, "E302", {"start": v(12.21, 13.82) * mm, "mid": v(9.08, 11.34) * mm, "end": v(6.22, 8.56) * mm});
            skArc(sketch, "E303", {"start": v(6.22, 8.56) * mm, "mid": v(5.77, 8.1) * mm, "end": v(5.61, 7.5) * mm});
            skArc(sketch, "E304", {"start": v(4.59, 6.54) * mm, "mid": v(5.2, 6.9) * mm, "end": v(5.61, 7.5) * mm});
            skArc(sketch, "E305", {"start": v(0.73, 5.73) * mm, "mid": v(2.69, 6) * mm, "end": v(4.59, 6.54) * mm});
            skLineSegment(sketch, "E306", {"start": v(-4.8, 7.35) * mm, "end": v(-3.91, 8.13) * mm});
            skLineSegment(sketch, "E307", {"start": v(5.61, 7.5) * mm, "end": v(4.74, 8.25) * mm});
            skLineSegment(sketch, "E308", {"start": v(-3.91, 8.13) * mm, "end": v(-2.34, 15.2) * mm});
            skArc(sketch, "E309", {"start": v(-2.34, 15.2) * mm, "mid": v(-2.25, 16.36) * mm, "end": v(-2.5, 17.48) * mm});
            skLineSegment(sketch, "E310", {"start": v(-2.5, 17.48) * mm, "end": v(-3, 17.48) * mm});
            skLineSegment(sketch, "E311", {"start": v(-3, 17.48) * mm, "end": v(-4.4, 21.08) * mm});
            skArc(sketch, "E312", {"start": v(-4.35, 21.21) * mm, "mid": v(-4.4, 21.15) * mm, "end": v(-4.4, 21.08) * mm});
            skArc(sketch, "E313", {"start": v(-4.2, 21.21) * mm, "mid": v(-4.28, 21.24) * mm, "end": v(-4.35, 21.21) * mm});
            skArc(sketch, "E314", {"start": v(-2.69, 19.13) * mm, "mid": v(-3.35, 20.24) * mm, "end": v(-4.2, 21.21) * mm});
            skArc(sketch, "E315", {"start": v(-2.69, 19.13) * mm, "mid": v(-2.55, 19.07) * mm, "end": v(-2.42, 19.13) * mm});
            skArc(sketch, "E316", {"start": v(-2.42, 19.45) * mm, "mid": v(-2.44, 19.3) * mm, "end": v(-2.42, 19.13) * mm});
            skArc(sketch, "E317", {"start": v(-2.1, 19.08) * mm, "mid": v(-2.24, 19.29) * mm, "end": v(-2.42, 19.45) * mm});
            skArc(sketch, "E318", {"start": v(-1.43, 16.6) * mm, "mid": v(-1.74, 17.85) * mm, "end": v(-2.1, 19.08) * mm});
            skArc(sketch, "E319", {"start": v(3.46, 16.35) * mm, "mid": v(1.04, 16.96) * mm, "end": v(-1.43, 16.6) * mm});
            skLineSegment(sketch, "E320", {"start": v(3.46, 16.35) * mm, "end": v(4.74, 8.25) * mm});
            skCircle(sketch, "E321", {"center": v(-0.03, -0.04) * mm, "radius": 2.77 * mm});
            skArc(sketch, "E322", {"start": v(-1.45, 2.65) * mm, "mid": v(-1, 2.78) * mm, "end": v(-0.63, 3.1) * mm});
            skArc(sketch, "E323", {"start": v(-1.87, 3.06) * mm, "mid": v(-1.7, 2.82) * mm, "end": v(-1.45, 2.65) * mm});
            skArc(sketch, "E324", {"start": v(-1.87, 3.06) * mm, "mid": v(-2.11, 3.26) * mm, "end": v(-2.42, 3.3) * mm});
            skArc(sketch, "E325", {"start": v(-2.97, 3.7) * mm, "mid": v(-2.76, 3.4) * mm, "end": v(-2.42, 3.3) * mm});
            skArc(sketch, "E326", {"start": v(-2.97, 3.7) * mm, "mid": v(-3.03, 3.92) * mm, "end": v(-3.16, 4.12) * mm});
            skArc(sketch, "E327", {"start": v(-3.16, 4.12) * mm, "mid": v(-3.5, 4.29) * mm, "end": v(-3.87, 4.35) * mm});
            skArc(sketch, "E328", {"start": v(-3.87, 4.35) * mm, "mid": v(-4.22, 4.67) * mm, "end": v(-4.57, 4.99) * mm});
            skArc(sketch, "E329", {"start": v(-4.57, 4.99) * mm, "mid": v(-4.77, 5.04) * mm, "end": v(-4.97, 4.99) * mm});
            skArc(sketch, "E330", {"start": v(-4.97, 4.99) * mm, "mid": v(-5.14, 5.16) * mm, "end": v(-5.37, 5.25) * mm});
            skArc(sketch, "E331", {"start": v(-5.37, 5.25) * mm, "mid": v(-5.42, 5.25) * mm, "end": v(-5.46, 5.23) * mm});
            skArc(sketch, "E332", {"start": v(-4.9, 4.32) * mm, "mid": v(-5.16, 4.79) * mm, "end": v(-5.46, 5.23) * mm});
            skArc(sketch, "E333", {"start": v(-4.9, 4.32) * mm, "mid": v(-4.43, 3.68) * mm, "end": v(-3.89, 3.1) * mm});
            skArc(sketch, "E334", {"start": v(-3.89, 3.1) * mm, "mid": v(-3.44, 2.3) * mm, "end": v(-2.82, 1.64) * mm});
            skArc(sketch, "E335", {"start": v(-3, 0.95) * mm, "mid": v(-2.83, 1.27) * mm, "end": v(-2.82, 1.64) * mm});
            skArc(sketch, "E336", {"start": v(-3, 0.95) * mm, "mid": v(-3.7, 0.73) * mm, "end": v(-4.36, 0.45) * mm});
            skArc(sketch, "E337", {"start": v(-5.36, 0.45) * mm, "mid": v(-4.86, 0.4) * mm, "end": v(-4.36, 0.45) * mm});
            skArc(sketch, "E338", {"start": v(-5.36, 0.45) * mm, "mid": v(-5.72, 0.56) * mm, "end": v(-6.08, 0.45) * mm});
            skArc(sketch, "E339", {"start": v(-6.08, 0.45) * mm, "mid": v(-6.4, 0.28) * mm, "end": v(-6.69, 0.07) * mm});
            skArc(sketch, "E340", {"start": v(-6.69, 0.07) * mm, "mid": v(-7.04, 0.05) * mm, "end": v(-7.39, -0.04) * mm});
            skArc(sketch, "E341", {"start": v(-7.39, -0.04) * mm, "mid": v(-7.6, -0.05) * mm, "end": v(-7.78, -0.14) * mm});
            skArc(sketch, "E342", {"start": v(-7.78, -0.14) * mm, "mid": v(-7.93, -0.16) * mm, "end": v(-8.07, -0.22) * mm});
            skArc(sketch, "E343", {"start": v(-8.07, -0.22) * mm, "mid": v(-8.1, -0.35) * mm, "end": v(-8, -0.45) * mm});
            skArc(sketch, "E344", {"start": v(-8, -0.45) * mm, "mid": v(-7.48, -0.48) * mm, "end": v(-6.96, -0.5) * mm});
            skArc(sketch, "E345", {"start": v(-6.96, -0.5) * mm, "mid": v(-6.48, -0.57) * mm, "end": v(-6, -0.61) * mm});
            skArc(sketch, "E346", {"start": v(-6, -0.61) * mm, "mid": v(-5.63, -0.76) * mm, "end": v(-5.23, -0.72) * mm});
            skArc(sketch, "E347", {"start": v(-4.95, -0.72) * mm, "mid": v(-5.1, -0.67) * mm, "end": v(-5.23, -0.72) * mm});
            skArc(sketch, "E348", {"start": v(-4.95, -0.72) * mm, "mid": v(-4.62, -0.9) * mm, "end": v(-4.23, -0.87) * mm});
            skArc(sketch, "E349", {"start": v(-3.57, -0.81) * mm, "mid": v(-3.9, -0.74) * mm, "end": v(-4.23, -0.87) * mm});
            skArc(sketch, "E350", {"start": v(-2.88, -1.27) * mm, "mid": v(-3.21, -1.03) * mm, "end": v(-3.57, -0.81) * mm});
            skArc(sketch, "E351", {"start": v(-2.88, -1.88) * mm, "mid": v(-2.77, -1.58) * mm, "end": v(-2.88, -1.27) * mm});
            skArc(sketch, "E352", {"start": v(-3.53, -2.44) * mm, "mid": v(-3.15, -2.23) * mm, "end": v(-2.88, -1.88) * mm});
            skArc(sketch, "E353", {"start": v(-3.53, -2.44) * mm, "mid": v(-3.68, -2.5) * mm, "end": v(-3.7, -2.66) * mm});
            skArc(sketch, "E354", {"start": v(-4.18, -3.64) * mm, "mid": v(-3.92, -3.16) * mm, "end": v(-3.7, -2.66) * mm});
            skArc(sketch, "E355", {"start": v(-4.18, -3.64) * mm, "mid": v(-4.52, -3.9) * mm, "end": v(-4.78, -4.25) * mm});
            skArc(sketch, "E356", {"start": v(-4.78, -4.25) * mm, "mid": v(-5.46, -4.96) * mm, "end": v(-5.84, -5.86) * mm});
            skArc(sketch, "E357", {"start": v(-5.84, -5.86) * mm, "mid": v(-5.66, -5.87) * mm, "end": v(-5.51, -5.76) * mm});
            skArc(sketch, "E358", {"start": v(-4.78, -5) * mm, "mid": v(-5.22, -5.3) * mm, "end": v(-5.51, -5.76) * mm});
            skArc(sketch, "E359", {"start": v(-4.78, -5) * mm, "mid": v(-4.4, -4.9) * mm, "end": v(-4.06, -4.71) * mm});
            skArc(sketch, "E360", {"start": v(-3.38, -4.03) * mm, "mid": v(-3.78, -4.3) * mm, "end": v(-4.06, -4.71) * mm});
            skArc(sketch, "E361", {"start": v(-2.43, -3.7) * mm, "mid": v(-2.91, -3.85) * mm, "end": v(-3.38, -4.03) * mm});
            skArc(sketch, "E362", {"start": v(-2.43, -3.7) * mm, "mid": v(-2.31, -3.65) * mm, "end": v(-2.24, -3.54) * mm});
            skArc(sketch, "E363", {"start": v(-1.64, -2.88) * mm, "mid": v(-1.98, -3.17) * mm, "end": v(-2.24, -3.54) * mm});
            skArc(sketch, "E364", {"start": v(-1.1, -2.98) * mm, "mid": v(-1.37, -2.9) * mm, "end": v(-1.64, -2.88) * mm});
            skArc(sketch, "E365", {"start": v(-0.56, -3.64) * mm, "mid": v(-0.8, -3.28) * mm, "end": v(-1.1, -2.98) * mm});
            skArc(sketch, "E366", {"start": v(-0.6, -4.5) * mm, "mid": v(-0.52, -4.07) * mm, "end": v(-0.56, -3.64) * mm});
            skArc(sketch, "E367", {"start": v(-0.6, -4.5) * mm, "mid": v(-0.7, -4.84) * mm, "end": v(-0.67, -5.2) * mm});
            skArc(sketch, "E368", {"start": v(-0.42, -6) * mm, "mid": v(-0.5, -5.59) * mm, "end": v(-0.67, -5.2) * mm});
            skArc(sketch, "E369", {"start": v(-0.42, -7.36) * mm, "mid": v(-0.41, -6.68) * mm, "end": v(-0.42, -6) * mm});
            skArc(sketch, "E370", {"start": v(-0.42, -7.36) * mm, "mid": v(-0.34, -7.64) * mm, "end": v(-0.15, -7.86) * mm});
            skArc(sketch, "E371", {"start": v(-0.15, -7.86) * mm, "mid": v(0, -7.82) * mm, "end": v(0.07, -7.7) * mm});
            skArc(sketch, "E372", {"start": v(0.07, -7.7) * mm, "mid": v(0.15, -7.2) * mm, "end": v(0.15, -6.7) * mm});
            skArc(sketch, "E373", {"start": v(0.15, -6.7) * mm, "mid": v(0.23, -6.56) * mm, "end": v(0.25, -6.4) * mm});
            skArc(sketch, "E374", {"start": v(0.25, -6.4) * mm, "mid": v(0.34, -6.3) * mm, "end": v(0.36, -6.16) * mm});
            skArc(sketch, "E375", {"start": v(0.36, -6.16) * mm, "mid": v(0.4, -5.44) * mm, "end": v(0.36, -4.71) * mm});
            skArc(sketch, "E376", {"start": v(0.36, -4.71) * mm, "mid": v(0.45, -4.62) * mm, "end": v(0.51, -4.5) * mm});
            skArc(sketch, "E377", {"start": v(0.51, -4.5) * mm, "mid": v(0.59, -4.38) * mm, "end": v(0.62, -4.25) * mm});
            skArc(sketch, "E378", {"start": v(0.62, -4.25) * mm, "mid": v(0.72, -4.07) * mm, "end": v(0.72, -3.87) * mm});
            skArc(sketch, "E379", {"start": v(0.82, -3.36) * mm, "mid": v(0.73, -3.6) * mm, "end": v(0.72, -3.87) * mm});
            skArc(sketch, "E380", {"start": v(1.26, -2.88) * mm, "mid": v(1.01, -3.1) * mm, "end": v(0.82, -3.36) * mm});
            skArc(sketch, "E381", {"start": v(1.83, -2.94) * mm, "mid": v(1.55, -2.86) * mm, "end": v(1.26, -2.88) * mm});
            skArc(sketch, "E382", {"start": v(2.36, -3.46) * mm, "mid": v(2.12, -3.17) * mm, "end": v(1.83, -2.94) * mm});
            skArc(sketch, "E383", {"start": v(2.36, -3.46) * mm, "mid": v(2.48, -3.6) * mm, "end": v(2.65, -3.64) * mm});
            skArc(sketch, "E384", {"start": v(3.37, -4.18) * mm, "mid": v(3.05, -3.86) * mm, "end": v(2.65, -3.64) * mm});
            skArc(sketch, "E385", {"start": v(3.9, -4.71) * mm, "mid": v(3.63, -4.44) * mm, "end": v(3.37, -4.18) * mm});
            skArc(sketch, "E386", {"start": v(3.9, -4.71) * mm, "mid": v(4, -4.72) * mm, "end": v(4.1, -4.71) * mm});
            skArc(sketch, "E387", {"start": v(4.78, -5.26) * mm, "mid": v(4.48, -4.94) * mm, "end": v(4.1, -4.71) * mm});
            skArc(sketch, "E388", {"start": v(4.78, -5.26) * mm, "mid": v(4.99, -5.42) * mm, "end": v(5.23, -5.52) * mm});
            skArc(sketch, "E389", {"start": v(5.23, -5.52) * mm, "mid": v(5.57, -5.57) * mm, "end": v(5.91, -5.52) * mm});
            skArc(sketch, "E390", {"start": v(5.91, -5.52) * mm, "mid": v(5.9, -5.36) * mm, "end": v(5.78, -5.26) * mm});
            skArc(sketch, "E391", {"start": v(5.09, -4.57) * mm, "mid": v(5.38, -4.96) * mm, "end": v(5.78, -5.26) * mm});
            skArc(sketch, "E392", {"start": v(5, -4.25) * mm, "mid": v(5.05, -4.4) * mm, "end": v(5.09, -4.57) * mm});
            skArc(sketch, "E393", {"start": v(5, -4.25) * mm, "mid": v(4.67, -3.8) * mm, "end": v(4.23, -3.45) * mm});
            skArc(sketch, "E394", {"start": v(4.23, -3.45) * mm, "mid": v(4.2, -3.17) * mm, "end": v(4.1, -2.9) * mm});
            skArc(sketch, "E395", {"start": v(3.06, -1.59) * mm, "mid": v(3.52, -2.3) * mm, "end": v(4.1, -2.9) * mm});
            skArc(sketch, "E396", {"start": v(3.06, -1.02) * mm, "mid": v(3.02, -1.3) * mm, "end": v(3.06, -1.59) * mm});
            skArc(sketch, "E397", {"start": v(3.28, -0.82) * mm, "mid": v(3.16, -0.9) * mm, "end": v(3.06, -1.02) * mm});
            skArc(sketch, "E398", {"start": v(3.28, -0.82) * mm, "mid": v(3.54, -0.8) * mm, "end": v(3.8, -0.75) * mm});
            skArc(sketch, "E399", {"start": v(3.8, -0.75) * mm, "mid": v(4.1, -0.57) * mm, "end": v(4.39, -0.35) * mm});
            skArc(sketch, "E400", {"start": v(4.89, -0.26) * mm, "mid": v(4.63, -0.26) * mm, "end": v(4.39, -0.35) * mm});
            skArc(sketch, "E401", {"start": v(4.89, -0.26) * mm, "mid": v(5.1, -0.35) * mm, "end": v(5.32, -0.35) * mm});
            skArc(sketch, "E402", {"start": v(5.32, -0.35) * mm, "mid": v(5.65, -0.31) * mm, "end": v(5.98, -0.23) * mm});
            skArc(sketch, "E403", {"start": v(6.19, -0.25) * mm, "mid": v(6.08, -0.22) * mm, "end": v(5.98, -0.23) * mm});
            skArc(sketch, "E404", {"start": v(6.19, -0.25) * mm, "mid": v(6.4, -0.32) * mm, "end": v(6.63, -0.3) * mm});
            skArc(sketch, "E405", {"start": v(7.08, -0.23) * mm, "mid": v(6.85, -0.24) * mm, "end": v(6.63, -0.3) * mm});
            skArc(sketch, "E406", {"start": v(7.08, -0.23) * mm, "mid": v(7.5, -0.3) * mm, "end": v(7.9, -0.25) * mm});
            skArc(sketch, "E407", {"start": v(8.17, -0.23) * mm, "mid": v(8.04, -0.22) * mm, "end": v(7.9, -0.25) * mm});
            skArc(sketch, "E408", {"start": v(8.17, -0.23) * mm, "mid": v(8.25, -0.18) * mm, "end": v(8.29, -0.1) * mm});
            skArc(sketch, "E409", {"start": v(8.29, -0.1) * mm, "mid": v(8.35, -0.07) * mm, "end": v(8.37, 0) * mm});
            skArc(sketch, "E410", {"start": v(8.37, 0) * mm, "mid": v(8.33, 0.04) * mm, "end": v(8.29, 0.09) * mm});
            skArc(sketch, "E411", {"start": v(8.29, 0.09) * mm, "mid": v(8.24, 0.15) * mm, "end": v(8.17, 0.2) * mm});
            skArc(sketch, "E412", {"start": v(8.17, 0.2) * mm, "mid": v(8.1, 0.2) * mm, "end": v(8, 0.2) * mm});
            skArc(sketch, "E413", {"start": v(8, 0.2) * mm, "mid": v(7.96, 0.24) * mm, "end": v(7.9, 0.28) * mm});
            skArc(sketch, "E414", {"start": v(7.9, 0.28) * mm, "mid": v(7.78, 0.28) * mm, "end": v(7.67, 0.24) * mm});
            skArc(sketch, "E415", {"start": v(7.14, 0.17) * mm, "mid": v(7.4, 0.2) * mm, "end": v(7.67, 0.24) * mm});
            skArc(sketch, "E416", {"start": v(7.14, 0.17) * mm, "mid": v(7.04, 0.26) * mm, "end": v(6.9, 0.28) * mm});
            skArc(sketch, "E417", {"start": v(6.9, 0.28) * mm, "mid": v(6.74, 0.32) * mm, "end": v(6.57, 0.28) * mm});
            skArc(sketch, "E418", {"start": v(6.34, 0.2) * mm, "mid": v(6.47, 0.2) * mm, "end": v(6.57, 0.28) * mm});
            skArc(sketch, "E419", {"start": v(6.34, 0.2) * mm, "mid": v(6.24, 0.27) * mm, "end": v(6.12, 0.33) * mm});
            skArc(sketch, "E420", {"start": v(6.12, 0.33) * mm, "mid": v(6.01, 0.4) * mm, "end": v(5.9, 0.45) * mm});
            skArc(sketch, "E421", {"start": v(5.9, 0.45) * mm, "mid": v(5.82, 0.53) * mm, "end": v(5.71, 0.56) * mm});
            skArc(sketch, "E422", {"start": v(5.71, 0.56) * mm, "mid": v(5.61, 0.52) * mm, "end": v(5.53, 0.45) * mm});
            skArc(sketch, "E423", {"start": v(5.53, 0.45) * mm, "mid": v(5.4, 0.43) * mm, "end": v(5.3, 0.36) * mm});
            skArc(sketch, "E424", {"start": v(5.3, 0.36) * mm, "mid": v(5.18, 0.32) * mm, "end": v(5.09, 0.24) * mm});
            skArc(sketch, "E425", {"start": v(4.93, 0.2) * mm, "mid": v(5, 0.21) * mm, "end": v(5.09, 0.24) * mm});
            skArc(sketch, "E426", {"start": v(4.73, 0.28) * mm, "mid": v(4.82, 0.22) * mm, "end": v(4.93, 0.2) * mm});
            skArc(sketch, "E427", {"start": v(4.33, 0.64) * mm, "mid": v(4.53, 0.46) * mm, "end": v(4.73, 0.28) * mm});
            skArc(sketch, "E428", {"start": v(4.33, 0.64) * mm, "mid": v(3.79, 0.74) * mm, "end": v(3.24, 0.76) * mm});
            skArc(sketch, "E429", {"start": v(3.06, 0.98) * mm, "mid": v(3.1, 0.82) * mm, "end": v(3.24, 0.76) * mm});
            skArc(sketch, "E430", {"start": v(3.14, 1.53) * mm, "mid": v(3.08, 1.26) * mm, "end": v(3.06, 0.98) * mm});
            skArc(sketch, "E431", {"start": v(4.37, 2.95) * mm, "mid": v(3.68, 2.3) * mm, "end": v(3.14, 1.53) * mm});
            skArc(sketch, "E432", {"start": v(4.37, 2.95) * mm, "mid": v(4.78, 3.38) * mm, "end": v(5.09, 3.89) * mm});
            skArc(sketch, "E433", {"start": v(5.56, 4.58) * mm, "mid": v(5.3, 4.25) * mm, "end": v(5.09, 3.89) * mm});
            skArc(sketch, "E434", {"start": v(5.56, 4.58) * mm, "mid": v(5.58, 4.82) * mm, "end": v(5.56, 5.05) * mm});
            skArc(sketch, "E435", {"start": v(5.9, 5.46) * mm, "mid": v(5.72, 5.26) * mm, "end": v(5.56, 5.05) * mm});
            skArc(sketch, "E436", {"start": v(5.9, 5.46) * mm, "mid": v(5.92, 5.58) * mm, "end": v(5.9, 5.69) * mm});
            skArc(sketch, "E437", {"start": v(5.9, 5.69) * mm, "mid": v(5.77, 5.7) * mm, "end": v(5.65, 5.69) * mm});
            skArc(sketch, "E438", {"start": v(5.65, 5.69) * mm, "mid": v(5.41, 5.47) * mm, "end": v(5.3, 5.16) * mm});
            skArc(sketch, "E439", {"start": v(5.3, 5.16) * mm, "mid": v(4.98, 4.95) * mm, "end": v(4.67, 4.72) * mm});
            skArc(sketch, "E440", {"start": v(4.67, 4.72) * mm, "mid": v(4.4, 4.64) * mm, "end": v(4.2, 4.47) * mm});
            skArc(sketch, "E441", {"start": v(4.2, 4.47) * mm, "mid": v(3.98, 4.18) * mm, "end": v(3.9, 3.82) * mm});
            skArc(sketch, "E442", {"start": v(3.64, 3.59) * mm, "mid": v(3.8, 3.67) * mm, "end": v(3.9, 3.82) * mm});
            skArc(sketch, "E443", {"start": v(3.64, 3.59) * mm, "mid": v(3.23, 3.6) * mm, "end": v(2.83, 3.54) * mm});
            skArc(sketch, "E444", {"start": v(2.83, 3.54) * mm, "mid": v(2.72, 3.46) * mm, "end": v(2.63, 3.35) * mm});
            skArc(sketch, "E445", {"start": v(1.73, 2.64) * mm, "mid": v(2.22, 2.95) * mm, "end": v(2.63, 3.35) * mm});
            skArc(sketch, "E446", {"start": v(1.28, 2.78) * mm, "mid": v(1.49, 2.65) * mm, "end": v(1.73, 2.64) * mm});
            skArc(sketch, "E447", {"start": v(0.95, 3.26) * mm, "mid": v(1.1, 3.01) * mm, "end": v(1.28, 2.78) * mm});
            skArc(sketch, "E448", {"start": v(0.95, 3.26) * mm, "mid": v(1.01, 3.54) * mm, "end": v(1.04, 3.84) * mm});
            skArc(sketch, "E449", {"start": v(1.04, 3.84) * mm, "mid": v(0.99, 4.19) * mm, "end": v(0.88, 4.53) * mm});
            skArc(sketch, "E450", {"start": v(0.73, 5.73) * mm, "mid": v(0.77, 5.12) * mm, "end": v(0.88, 4.53) * mm});
            skArc(sketch, "E451", {"start": v(-0.22, 5.19) * mm, "mid": v(-0.08, 5.47) * mm, "end": v(-0.03, 5.78) * mm});
            skArc(sketch, "E452", {"start": v(-0.22, 5.19) * mm, "mid": v(-0.4, 4.82) * mm, "end": v(-0.52, 4.42) * mm});
            skArc(sketch, "E453", {"start": v(-0.52, 4.42) * mm, "mid": v(-0.65, 3.77) * mm, "end": v(-0.63, 3.1) * mm});
            skLineSegment(sketch, "E454", {"start": v(0.3, 12.78) * mm, "end": v(0.2, 8.56) * mm});
            skLineSegment(sketch, "E455", {"start": v(0.2, 8.56) * mm, "end": v(0.7, 8.55) * mm});
            skLineSegment(sketch, "E456", {"start": v(0.7, 8.55) * mm, "end": v(0.86, 12.8) * mm});
            skArc(sketch, "E457", {"start": v(0.3, 12.78) * mm, "mid": v(-0.71, 12.7) * mm, "end": v(-1.7, 12.43) * mm});
            skArc(sketch, "E458", {"start": v(2.84, 12.43) * mm, "mid": v(1.87, 12.7) * mm, "end": v(0.86, 12.8) * mm});
            skArc(sketch, "E459", {"start": v(-1.93, 13.58) * mm, "mid": v(-1.85, 13) * mm, "end": v(-1.7, 12.43) * mm});
            skArc(sketch, "E460", {"start": v(0.3, 14.08) * mm, "mid": v(-0.84, 13.95) * mm, "end": v(-1.93, 13.58) * mm});
            skArc(sketch, "E461", {"start": v(2.84, 12.43) * mm, "mid": v(3.07, 13.02) * mm, "end": v(3.12, 13.66) * mm});
            skArc(sketch, "E462", {"start": v(3.12, 13.66) * mm, "mid": v(2.04, 13.95) * mm, "end": v(0.92, 14.08) * mm});
            skArc(sketch, "E463", {"start": v(0.3, 14.08) * mm, "mid": v(0.42, 14.67) * mm, "end": v(0.47, 15.28) * mm});
            skArc(sketch, "E464", {"start": v(0.92, 14.08) * mm, "mid": v(0.94, 14.68) * mm, "end": v(0.92, 15.28) * mm});
            skArc(sketch, "E465", {"start": v(0.92, 15.28) * mm, "mid": v(0.7, 15.33) * mm, "end": v(0.47, 15.28) * mm});
            skArc(sketch, "E466", {"start": v(13.08, 13.23) * mm, "mid": v(9.66, 10.5) * mm, "end": v(6.51, 7.45) * mm});
            skArc(sketch, "E467", {"start": v(15.77, 16.35) * mm, "mid": v(14.29, 14.9) * mm, "end": v(13.08, 13.23) * mm});
            skArc(sketch, "E468", {"start": v(8.46, 2.64) * mm, "mid": v(11.72, 6.71) * mm, "end": v(14.4, 11.2) * mm});
            skArc(sketch, "E469", {"start": v(14.4, 11.2) * mm, "mid": v(16.35, 13.01) * mm, "end": v(17.77, 15.28) * mm});
            skLineSegment(sketch, "E470", {"start": v(6.51, 7.45) * mm, "end": v(8.46, 2.64) * mm});
            skLineSegment(sketch, "E471", {"start": v(17.77, 15.28) * mm, "end": v(15.77, 16.35) * mm});
            skArc(sketch, "E472", {"start": v(-16.3, 14.77) * mm, "mid": v(-15.08, 12.63) * mm, "end": v(-13.31, 10.91) * mm});
            skArc(sketch, "E473", {"start": v(-11.75, 12.84) * mm, "mid": v(-12.84, 14.5) * mm, "end": v(-14.24, 15.91) * mm});
            skArc(sketch, "E474", {"start": v(-13.31, 10.91) * mm, "mid": v(-10.9, 6.58) * mm, "end": v(-8.09, 2.5) * mm});
            skArc(sketch, "E475", {"start": v(-5.71, 7.3) * mm, "mid": v(-8.52, 10.3) * mm, "end": v(-11.75, 12.84) * mm});
            skLineSegment(sketch, "E476", {"start": v(-16.3, 14.77) * mm, "end": v(-14.24, 15.91) * mm});
            skLineSegment(sketch, "E477", {"start": v(-8.09, 2.5) * mm, "end": v(-5.71, 7.3) * mm});
            skLineSegment(sketch, "E478", {"start": v(25.2, -18.3) * mm, "end": v(25.24, -20.7) * mm});
            skLineSegment(sketch, "E479", {"start": v(-25.66, -20.7) * mm, "end": v(-25.66, -18.9) * mm});
            skArc(sketch, "E480", {"start": v(-3.91, 8.13) * mm, "mid": v(-3.26, 7.6) * mm, "end": v(-2.5, 7.24) * mm});
            skArc(sketch, "E481", {"start": v(-2.5, 7.24) * mm, "mid": v(-1.27, 7.06) * mm, "end": v(-0.03, 7.03) * mm});
            skArc(sketch, "E482", {"start": v(2.96, 7.33) * mm, "mid": v(3.95, 7.6) * mm, "end": v(4.74, 8.25) * mm});
            skArc(sketch, "E483", {"start": v(-0.03, 7.03) * mm, "mid": v(1.47, 7.08) * mm, "end": v(2.96, 7.33) * mm});
            skArc(sketch, "E484", {"start": v(18.89, 21.82) * mm, "mid": v(20.07, 20.92) * mm, "end": v(21.29, 20.07) * mm});
            skArc(sketch, "E485", {"start": v(21.4, 20.66) * mm, "mid": v(20.48, 21.41) * mm, "end": v(19.54, 22.13) * mm});
            skArc(sketch, "E486", {"start": v(-17.38, 21.52) * mm, "mid": v(-18.42, 20.9) * mm, "end": v(-19.38, 20.14) * mm});
            skArc(sketch, "E487", {"start": v(-19.38, 19.62) * mm, "mid": v(-18.05, 20.41) * mm, "end": v(-16.83, 21.38) * mm});
            skSolve(sketch);
        }
        {
            var Q0;
            Q0=makeQuery(id+"F2.imprint","IMPRINT",FACE,{"disambiguationData":[TD([[makeQuery(id+"F2.imprint","IMPRINT",EDGE,{"derivedFrom":sQuery(id+"F2.wireOp",EDGE,"E472")}),1.0]])]});
            var Q1;
            Q1=makeQuery(id+"F2.imprint","IMPRINT",FACE,{"disambiguationData":[TD([[makeQuery(id+"F2.imprint","IMPRINT",EDGE,{"derivedFrom":sQuery(id+"F2.wireOp",EDGE,"E466")}),1.0]])]});
            var Q2;
            Q2=makeQuery(id+"F2.imprint","IMPRINT",FACE,{"disambiguationData":[TD([[makeQuery(id+"F2.imprint","IMPRINT",EDGE,{"derivedFrom":sQuery(id+"F2.wireOp",EDGE,"E454")}),1.0]])]});
            var Q3;
            Q3=makeQuery(id+"F2.imprint","IMPRINT",FACE,{"disambiguationData":[TD([[makeQuery(id+"F2.imprint","IMPRINT",EDGE,{"derivedFrom":sQuery(id+"F2.wireOp",EDGE,"E266")}),1.0]])]});
            var Q4;
            Q4=makeQuery(id+"F2.imprint","IMPRINT",FACE,{"disambiguationData":[TD([[makeQuery(id+"F2.imprint","IMPRINT",EDGE,{"derivedFrom":sQuery(id+"F2.wireOp",EDGE,"E286")}),-1.0]])]});
            var Q5;
            Q5=makeQuery(id+"F2.imprint","IMPRINT",FACE,{"disambiguationData":[TD([[makeQuery(id+"F2.imprint","IMPRINT",EDGE,{"derivedFrom":sQuery(id+"F2.wireOp",EDGE,"E254")}),-1.0]])]});
            extrude(context, id + "F3", {"entities" : qUnion([Q0, Q1, Q2, Q3, Q4, Q5]), "depth" : 7.5 * mm});
        }
        {
            var Q0;
            Q0=makeQuery(id+"F1.opExtrude","CAP_FACE",FACE,{"disambiguationData":[OSD([sQuery(id+"F0.wireOp",EDGE,"E12"),sQuery(id+"F0.wireOp",EDGE,"E13"),sQuery(id+"F0.wireOp",EDGE,"E14"),sQuery(id+"F0.wireOp",EDGE,"E15"),sQuery(id+"F0.wireOp",EDGE,"E16"),sQuery(id+"F0.wireOp",EDGE,"E17"),sQuery(id+"F0.wireOp",EDGE,"E18"),sQuery(id+"F0.wireOp",EDGE,"E19"),sQuery(id+"F0.wireOp",EDGE,"E20"),sQuery(id+"F0.wireOp",EDGE,"E21"),sQuery(id+"F0.wireOp",EDGE,"E22"),sQuery(id+"F0.wireOp",EDGE,"E23"),sQuery(id+"F0.wireOp",EDGE,"E24"),sQuery(id+"F0.wireOp",EDGE,"E25"),sQuery(id+"F0.wireOp",EDGE,"E26"),sQuery(id+"F0.wireOp",EDGE,"E28"),sQuery(id+"F0.wireOp",EDGE,"E29"),sQuery(id+"F0.wireOp",EDGE,"E31"),sQuery(id+"F0.wireOp",EDGE,"E33"),sQuery(id+"F0.wireOp",EDGE,"E34"),sQuery(id+"F0.wireOp",EDGE,"E35"),sQuery(id+"F0.wireOp",EDGE,"E36"),sQuery(id+"F0.wireOp",EDGE,"E37"),sQuery(id+"F0.wireOp",EDGE,"E38"),sQuery(id+"F0.wireOp",EDGE,"E39"),sQuery(id+"F0.wireOp",EDGE,"E40"),sQuery(id+"F0.wireOp",EDGE,"E53"),sQuery(id+"F0.wireOp",EDGE,"E55"),sQuery(id+"F0.wireOp",EDGE,"E56"),sQuery(id+"F0.wireOp",EDGE,"E57"),sQuery(id+"F0.wireOp",EDGE,"E58"),sQuery(id+"F0.wireOp",EDGE,"E59"),sQuery(id+"F0.wireOp",EDGE,"E60"),sQuery(id+"F0.wireOp",EDGE,"E61"),sQuery(id+"F0.wireOp",EDGE,"E78"),sQuery(id+"F0.wireOp",EDGE,"E79"),sQuery(id+"F0.wireOp",EDGE,"E80"),sQuery(id+"F0.wireOp",EDGE,"E81"),sQuery(id+"F0.wireOp",EDGE,"E82"),sQuery(id+"F0.wireOp",EDGE,"E83"),sQuery(id+"F0.wireOp",EDGE,"E84"),sQuery(id+"F0.wireOp",EDGE,"E85"),sQuery(id+"F0.wireOp",EDGE,"E86"),sQuery(id+"F0.wireOp",EDGE,"E87"),sQuery(id+"F0.wireOp",EDGE,"E88"),sQuery(id+"F0.wireOp",EDGE,"E89"),sQuery(id+"F0.wireOp",EDGE,"E90"),sQuery(id+"F0.wireOp",EDGE,"E91"),sQuery(id+"F0.wireOp",EDGE,"E92"),sQuery(id+"F0.wireOp",EDGE,"E93"),sQuery(id+"F0.wireOp",EDGE,"E94"),sQuery(id+"F0.wireOp",EDGE,"E95"),sQuery(id+"F0.wireOp",EDGE,"E96"),sQuery(id+"F0.wireOp",EDGE,"E97"),sQuery(id+"F0.wireOp",EDGE,"E98"),sQuery(id+"F0.wireOp",EDGE,"E99"),sQuery(id+"F0.wireOp",EDGE,"E100"),sQuery(id+"F0.wireOp",EDGE,"E101"),sQuery(id+"F0.wireOp",EDGE,"E102"),sQuery(id+"F0.wireOp",EDGE,"E103"),sQuery(id+"F0.wireOp",EDGE,"E104"),sQuery(id+"F0.wireOp",EDGE,"E105"),sQuery(id+"F0.wireOp",EDGE,"E106"),sQuery(id+"F0.wireOp",EDGE,"E107"),sQuery(id+"F0.wireOp",EDGE,"E108"),sQuery(id+"F0.wireOp",EDGE,"E109"),sQuery(id+"F0.wireOp",EDGE,"E110"),sQuery(id+"F0.wireOp",EDGE,"E111"),sQuery(id+"F0.wireOp",EDGE,"E112"),sQuery(id+"F0.wireOp",EDGE,"E113"),sQuery(id+"F0.wireOp",EDGE,"E114"),sQuery(id+"F0.wireOp",EDGE,"E115"),sQuery(id+"F0.wireOp",EDGE,"E116"),sQuery(id+"F0.wireOp",EDGE,"E117"),sQuery(id+"F0.wireOp",EDGE,"E118"),sQuery(id+"F0.wireOp",EDGE,"E119"),sQuery(id+"F0.wireOp",EDGE,"E120"),sQuery(id+"F0.wireOp",EDGE,"E121"),sQuery(id+"F0.wireOp",EDGE,"E122"),sQuery(id+"F0.wireOp",EDGE,"E123"),sQuery(id+"F0.wireOp",EDGE,"E124"),sQuery(id+"F0.wireOp",EDGE,"E125"),sQuery(id+"F0.wireOp",EDGE,"E126"),sQuery(id+"F0.wireOp",EDGE,"E127"),sQuery(id+"F0.wireOp",EDGE,"E128"),sQuery(id+"F0.wireOp",EDGE,"E129"),sQuery(id+"F0.wireOp",EDGE,"E130"),sQuery(id+"F0.wireOp",EDGE,"E131"),sQuery(id+"F0.wireOp",EDGE,"E132"),sQuery(id+"F0.wireOp",EDGE,"E133"),sQuery(id+"F0.wireOp",EDGE,"E134"),sQuery(id+"F0.wireOp",EDGE,"E135"),sQuery(id+"F0.wireOp",EDGE,"E136"),sQuery(id+"F0.wireOp",EDGE,"E137"),sQuery(id+"F0.wireOp",EDGE,"E138"),sQuery(id+"F0.wireOp",EDGE,"E139"),sQuery(id+"F0.wireOp",EDGE,"E140"),sQuery(id+"F0.wireOp",EDGE,"E141"),sQuery(id+"F0.wireOp",EDGE,"E142"),sQuery(id+"F0.wireOp",EDGE,"E143"),sQuery(id+"F0.wireOp",EDGE,"E144"),sQuery(id+"F0.wireOp",EDGE,"E145"),sQuery(id+"F0.wireOp",EDGE,"E146"),sQuery(id+"F0.wireOp",EDGE,"E147"),sQuery(id+"F0.wireOp",EDGE,"E148"),sQuery(id+"F0.wireOp",EDGE,"E149"),sQuery(id+"F0.wireOp",EDGE,"E150"),sQuery(id+"F0.wireOp",EDGE,"E151"),sQuery(id+"F0.wireOp",EDGE,"E152"),sQuery(id+"F0.wireOp",EDGE,"E153"),sQuery(id+"F0.wireOp",EDGE,"E154"),sQuery(id+"F0.wireOp",EDGE,"E155"),sQuery(id+"F0.wireOp",EDGE,"E156"),sQuery(id+"F0.wireOp",EDGE,"E157"),sQuery(id+"F0.wireOp",EDGE,"E158"),sQuery(id+"F0.wireOp",EDGE,"E159"),sQuery(id+"F0.wireOp",EDGE,"E160"),sQuery(id+"F0.wireOp",EDGE,"E161"),sQuery(id+"F0.wireOp",EDGE,"E162"),sQuery(id+"F0.wireOp",EDGE,"E163"),sQuery(id+"F0.wireOp",EDGE,"E164"),sQuery(id+"F0.wireOp",EDGE,"E165"),sQuery(id+"F0.wireOp",EDGE,"E166"),sQuery(id+"F0.wireOp",EDGE,"E167"),sQuery(id+"F0.wireOp",EDGE,"E168"),sQuery(id+"F0.wireOp",EDGE,"E169"),sQuery(id+"F0.wireOp",EDGE,"E170"),sQuery(id+"F0.wireOp",EDGE,"E171"),sQuery(id+"F0.wireOp",EDGE,"E172"),sQuery(id+"F0.wireOp",EDGE,"E173"),sQuery(id+"F0.wireOp",EDGE,"E174"),sQuery(id+"F0.wireOp",EDGE,"E175"),sQuery(id+"F0.wireOp",EDGE,"E176"),sQuery(id+"F0.wireOp",EDGE,"E177"),sQuery(id+"F0.wireOp",EDGE,"E178"),sQuery(id+"F0.wireOp",EDGE,"E179"),sQuery(id+"F0.wireOp",EDGE,"E180"),sQuery(id+"F0.wireOp",EDGE,"E181"),sQuery(id+"F0.wireOp",EDGE,"E182"),sQuery(id+"F0.wireOp",EDGE,"E183"),sQuery(id+"F0.wireOp",EDGE,"E184"),sQuery(id+"F0.wireOp",EDGE,"E185"),sQuery(id+"F0.wireOp",EDGE,"E186"),sQuery(id+"F0.wireOp",EDGE,"E187"),sQuery(id+"F0.wireOp",EDGE,"E188"),sQuery(id+"F0.wireOp",EDGE,"E189"),sQuery(id+"F0.wireOp",EDGE,"E190"),sQuery(id+"F0.wireOp",EDGE,"E191"),sQuery(id+"F0.wireOp",EDGE,"E192"),sQuery(id+"F0.wireOp",EDGE,"E193"),sQuery(id+"F0.wireOp",EDGE,"E194"),sQuery(id+"F0.wireOp",EDGE,"E195"),sQuery(id+"F0.wireOp",EDGE,"E196"),sQuery(id+"F0.wireOp",EDGE,"E197"),sQuery(id+"F0.wireOp",EDGE,"E198"),sQuery(id+"F0.wireOp",EDGE,"E199"),sQuery(id+"F0.wireOp",EDGE,"E200"),sQuery(id+"F0.wireOp",EDGE,"E201"),sQuery(id+"F0.wireOp",EDGE,"E202"),sQuery(id+"F0.wireOp",EDGE,"E203"),sQuery(id+"F0.wireOp",EDGE,"E204"),sQuery(id+"F0.wireOp",EDGE,"E205"),sQuery(id+"F0.wireOp",EDGE,"E206"),sQuery(id+"F0.wireOp",EDGE,"E207"),sQuery(id+"F0.wireOp",EDGE,"E208"),sQuery(id+"F0.wireOp",EDGE,"E209"),sQuery(id+"F0.wireOp",EDGE,"E222"),sQuery(id+"F0.wireOp",EDGE,"E223"),sQuery(id+"F0.wireOp",EDGE,"E224"),sQuery(id+"F0.wireOp",EDGE,"E225"),sQuery(id+"F0.wireOp",EDGE,"E226"),sQuery(id+"F0.wireOp",EDGE,"E227"),sQuery(id+"F0.wireOp",EDGE,"E228"),sQuery(id+"F0.wireOp",EDGE,"E229"),sQuery(id+"F0.wireOp",EDGE,"E230"),sQuery(id+"F0.wireOp",EDGE,"E231"),sQuery(id+"F0.wireOp",EDGE,"E232"),sQuery(id+"F0.wireOp",EDGE,"E233"),sQuery(id+"F0.wireOp",EDGE,"E234"),sQuery(id+"F0.wireOp",EDGE,"E235"),sQuery(id+"F0.wireOp",EDGE,"E240"),sQuery(id+"F0.wireOp",EDGE,"E243")])],"isStart":false});
            var sketch = newSketch(context, id + "F4", { "sketchPlane" : qUnion([Q0])});
            skLineSegment(sketch, "E488", {"start": v(-23.7, -18.24) * mm, "end": v(-23.38, -11.37) * mm});
            skArc(sketch, "E489", {"start": v(-23.38, -11.37) * mm, "mid": v(-23.44, -11.14) * mm, "end": v(-23.6, -10.98) * mm});
            skArc(sketch, "E490", {"start": v(-23.38, -10.9) * mm, "mid": v(-23.5, -10.93) * mm, "end": v(-23.6, -10.98) * mm});
            skLineSegment(sketch, "E491", {"start": v(-23.38, -10.9) * mm, "end": v(-20.94, -10.9) * mm});
            skArc(sketch, "E492", {"start": v(-20.34, -11.38) * mm, "mid": v(-20.59, -11.07) * mm, "end": v(-20.94, -10.9) * mm});
            skLineSegment(sketch, "E493", {"start": v(-20.34, -11.38) * mm, "end": v(-20.46, -14.86) * mm});
            skArc(sketch, "E494", {"start": v(-21.18, -15.68) * mm, "mid": v(-20.73, -15.35) * mm, "end": v(-20.46, -14.86) * mm});
            skLineSegment(sketch, "E495", {"start": v(-21.18, -15.68) * mm, "end": v(-21.98, -15.68) * mm});
            skArc(sketch, "E496", {"start": v(-21.98, -15.68) * mm, "mid": v(-22.14, -15.8) * mm, "end": v(-22.21, -16) * mm});
            skLineSegment(sketch, "E497", {"start": v(-22.21, -16) * mm, "end": v(-22.25, -18.28) * mm});
            skLineSegment(sketch, "E498", {"start": v(-22.25, -18.28) * mm, "end": v(-21.87, -18.69) * mm});
            skLineSegment(sketch, "E499", {"start": v(-21.87, -18.69) * mm, "end": v(-24.16, -18.69) * mm});
            skLineSegment(sketch, "E500", {"start": v(-24.16, -18.69) * mm, "end": v(-23.7, -18.24) * mm});
            skLineSegment(sketch, "E501", {"start": v(-20.82, -18.69) * mm, "end": v(-18.69, -18.69) * mm});
            skLineSegment(sketch, "E502", {"start": v(-18.69, -18.69) * mm, "end": v(-18.86, -18.41) * mm});
            skLineSegment(sketch, "E503", {"start": v(-18.86, -18.41) * mm, "end": v(-18.8, -15.9) * mm});
            skArc(sketch, "E504", {"start": v(-18.49, -15.9) * mm, "mid": v(-18.64, -15.8) * mm, "end": v(-18.8, -15.9) * mm});
            skLineSegment(sketch, "E505", {"start": v(-18.49, -15.9) * mm, "end": v(-18.49, -18.69) * mm});
            skLineSegment(sketch, "E506", {"start": v(-18.49, -18.69) * mm, "end": v(-16.9, -18.69) * mm});
            skLineSegment(sketch, "E507", {"start": v(-16.9, -18.69) * mm, "end": v(-17.15, -18.43) * mm});
            skLineSegment(sketch, "E508", {"start": v(-17.15, -18.43) * mm, "end": v(-17.06, -15.27) * mm});
            skArc(sketch, "E509", {"start": v(-17.06, -15.27) * mm, "mid": v(-17.12, -15.06) * mm, "end": v(-17.3, -14.92) * mm});
            skArc(sketch, "E510", {"start": v(-17.3, -14.92) * mm, "mid": v(-17.17, -14.75) * mm, "end": v(-17.06, -14.56) * mm});
            skLineSegment(sketch, "E511", {"start": v(-17.06, -14.56) * mm, "end": v(-16.93, -11.48) * mm});
            skArc(sketch, "E512", {"start": v(-16.93, -11.48) * mm, "mid": v(-17.1, -11.04) * mm, "end": v(-17.56, -10.87) * mm});
            skLineSegment(sketch, "E513", {"start": v(-17.56, -10.87) * mm, "end": v(-20.25, -10.87) * mm});
            skArc(sketch, "E514", {"start": v(-20.01, -11.13) * mm, "mid": v(-20.1, -10.98) * mm, "end": v(-20.25, -10.87) * mm});
            skLineSegment(sketch, "E515", {"start": v(-20.01, -11.13) * mm, "end": v(-20.28, -18.12) * mm});
            skLineSegment(sketch, "E516", {"start": v(-20.28, -18.12) * mm, "end": v(-20.82, -18.69) * mm});
            skLineSegment(sketch, "E517", {"start": v(-16.76, -18.69) * mm, "end": v(-15.12, -18.69) * mm});
            skLineSegment(sketch, "E518", {"start": v(-15.12, -18.69) * mm, "end": v(-15.36, -18.46) * mm});
            skLineSegment(sketch, "E519", {"start": v(-15.36, -18.46) * mm, "end": v(-15.33, -17.77) * mm});
            skArc(sketch, "E520", {"start": v(-15.2, -17.49) * mm, "mid": v(-15.3, -17.61) * mm, "end": v(-15.33, -17.77) * mm});
            skLineSegment(sketch, "E521", {"start": v(-15.2, -17.49) * mm, "end": v(-14.56, -17.49) * mm});
            skArc(sketch, "E522", {"start": v(-14.44, -17.54) * mm, "mid": v(-14.5, -17.5) * mm, "end": v(-14.56, -17.49) * mm});
            skLineSegment(sketch, "E523", {"start": v(-14.44, -17.54) * mm, "end": v(-14.44, -18.37) * mm});
            skLineSegment(sketch, "E524", {"start": v(-14.44, -18.37) * mm, "end": v(-14.44, -18.46) * mm});
            skLineSegment(sketch, "E525", {"start": v(-14.44, -18.46) * mm, "end": v(-14.65, -18.69) * mm});
            skLineSegment(sketch, "E526", {"start": v(-14.65, -18.69) * mm, "end": v(-12.95, -18.69) * mm});
            skLineSegment(sketch, "E527", {"start": v(-12.95, -18.69) * mm, "end": v(-13.16, -18.43) * mm});
            skLineSegment(sketch, "E528", {"start": v(-13.16, -18.43) * mm, "end": v(-13.51, -11.08) * mm});
            skArc(sketch, "E529", {"start": v(-13.41, -10.92) * mm, "mid": v(-13.49, -10.99) * mm, "end": v(-13.51, -11.08) * mm});
            skArc(sketch, "E530", {"start": v(-13.41, -10.92) * mm, "mid": v(-13.5, -10.82) * mm, "end": v(-13.61, -10.77) * mm});
            skLineSegment(sketch, "E531", {"start": v(-13.61, -10.77) * mm, "end": v(-15.66, -10.77) * mm});
            skArc(sketch, "E532", {"start": v(-15.66, -10.77) * mm, "mid": v(-15.78, -10.8) * mm, "end": v(-15.84, -10.92) * mm});
            skArc(sketch, "E533", {"start": v(-15.68, -11.02) * mm, "mid": v(-15.75, -10.96) * mm, "end": v(-15.84, -10.92) * mm});
            skLineSegment(sketch, "E534", {"start": v(-15.68, -11.02) * mm, "end": v(-16.62, -18.47) * mm});
            skLineSegment(sketch, "E535", {"start": v(-16.62, -18.47) * mm, "end": v(-16.76, -18.69) * mm});
            skLineSegment(sketch, "E536", {"start": v(-12.08, -11.12) * mm, "end": v(-12.3, -18.12) * mm});
            skPoint(sketch, "E536.endSnap0", {"position": v(-15.35, -18.12) * mm});
            skLineSegment(sketch, "E537", {"start": v(-12.3, -18.12) * mm, "end": v(-12.7, -18.57) * mm});
            skLineSegment(sketch, "E538", {"start": v(-12.7, -18.57) * mm, "end": v(-10.5, -18.57) * mm});
            skLineSegment(sketch, "E539", {"start": v(-10.5, -18.57) * mm, "end": v(-10.84, -18.21) * mm});
            skLineSegment(sketch, "E540", {"start": v(-10.84, -18.21) * mm, "end": v(-10.61, -11.18) * mm});
            skLineSegment(sketch, "E541", {"start": v(-10.61, -11.18) * mm, "end": v(-10.31, -10.8) * mm});
            skLineSegment(sketch, "E542", {"start": v(-10.31, -10.8) * mm, "end": v(-12.26, -10.8) * mm});
            skLineSegment(sketch, "E543", {"start": v(-12.26, -10.8) * mm, "end": v(-12.36, -10.8) * mm});
            skLineSegment(sketch, "E544", {"start": v(-12.36, -10.8) * mm, "end": v(-12.08, -11.12) * mm});
            skLineSegment(sketch, "E545", {"start": v(-10.18, -15.95) * mm, "end": v(-10.18, -18.09) * mm});
            skArc(sketch, "E546", {"start": v(-10.18, -18.09) * mm, "mid": v(-9.9, -18.38) * mm, "end": v(-9.54, -18.56) * mm});
            skArc(sketch, "E547", {"start": v(-10.18, -15.95) * mm, "mid": v(-10.02, -16.43) * mm, "end": v(-9.75, -16.85) * mm});
            skArc(sketch, "E548", {"start": v(-9.75, -16.85) * mm, "mid": v(-9.36, -16.95) * mm, "end": v(-8.97, -16.85) * mm});
            skArc(sketch, "E549", {"start": v(-8.97, -16.85) * mm, "mid": v(-8.82, -16.65) * mm, "end": v(-8.77, -16.4) * mm});
            skArc(sketch, "E550", {"start": v(-8.77, -16.4) * mm, "mid": v(-8.77, -16) * mm, "end": v(-8.85, -15.6) * mm});
            skArc(sketch, "E551", {"start": v(-8.85, -15.6) * mm, "mid": v(-8.89, -15.51) * mm, "end": v(-8.94, -15.42) * mm});
            skArc(sketch, "E552", {"start": v(-10.1, -14.26) * mm, "mid": v(-9.54, -14.87) * mm, "end": v(-8.94, -15.42) * mm});
            skLineSegment(sketch, "E553", {"start": v(-10.1, -14.26) * mm, "end": v(-10.1, -11.53) * mm});
            skArc(sketch, "E554", {"start": v(-9.48, -10.81) * mm, "mid": v(-9.87, -11.1) * mm, "end": v(-10.1, -11.53) * mm});
            skArc(sketch, "E555", {"start": v(-9.07, -10.73) * mm, "mid": v(-9.28, -10.75) * mm, "end": v(-9.48, -10.81) * mm});
            skLineSegment(sketch, "E556", {"start": v(-9.07, -10.73) * mm, "end": v(-7.9, -10.73) * mm});
            skArc(sketch, "E557", {"start": v(-7.34, -11.1) * mm, "mid": v(-7.59, -10.88) * mm, "end": v(-7.9, -10.73) * mm});
            skLineSegment(sketch, "E558", {"start": v(-7.34, -11.1) * mm, "end": v(-7.34, -13.11) * mm});
            skArc(sketch, "E559", {"start": v(-7.34, -13.11) * mm, "mid": v(-7.44, -12.81) * mm, "end": v(-7.57, -12.52) * mm});
            skArc(sketch, "E560", {"start": v(-7.57, -12.52) * mm, "mid": v(-7.73, -12.33) * mm, "end": v(-7.92, -12.18) * mm});
            skArc(sketch, "E561", {"start": v(-7.92, -12.18) * mm, "mid": v(-8.25, -12.13) * mm, "end": v(-8.56, -12.23) * mm});
            skArc(sketch, "E562", {"start": v(-8.56, -12.23) * mm, "mid": v(-8.64, -12.33) * mm, "end": v(-8.67, -12.47) * mm});
            skLineSegment(sketch, "E563", {"start": v(-8.67, -12.47) * mm, "end": v(-8.67, -13.38) * mm});
            skArc(sketch, "E564", {"start": v(-8.67, -13.38) * mm, "mid": v(-8.65, -13.46) * mm, "end": v(-8.6, -13.53) * mm});
            skArc(sketch, "E565", {"start": v(-7.48, -14.72) * mm, "mid": v(-8, -14.08) * mm, "end": v(-8.6, -13.53) * mm});
            skLineSegment(sketch, "E566", {"start": v(-7.48, -14.72) * mm, "end": v(-7.48, -17.8) * mm});
            skArc(sketch, "E567", {"start": v(-8.17, -18.56) * mm, "mid": v(-7.76, -18.25) * mm, "end": v(-7.48, -17.8) * mm});
            skLineSegment(sketch, "E568", {"start": v(-9.54, -18.56) * mm, "end": v(-8.17, -18.56) * mm});
            skLineSegment(sketch, "E569", {"start": v(-6.83, -11.14) * mm, "end": v(-7.03, -17.99) * mm});
            skLineSegment(sketch, "E570", {"start": v(-7.03, -17.99) * mm, "end": v(-7.54, -18.56) * mm});
            skLineSegment(sketch, "E571", {"start": v(-7.54, -18.56) * mm, "end": v(-4.04, -18.56) * mm});
            skLineSegment(sketch, "E572", {"start": v(-4.04, -18.56) * mm, "end": v(-4.01, -16.84) * mm});
            skLineSegment(sketch, "E573", {"start": v(-4.5, -17.3) * mm, "end": v(-5.49, -17.3) * mm});
            skArc(sketch, "E574", {"start": v(-4.5, -17.3) * mm, "mid": v(-4.23, -17.1) * mm, "end": v(-4.01, -16.84) * mm});
            skArc(sketch, "E575", {"start": v(-5.63, -17.25) * mm, "mid": v(-5.56, -17.29) * mm, "end": v(-5.49, -17.3) * mm});
            skArc(sketch, "E576", {"start": v(-5.65, -17.16) * mm, "mid": v(-5.65, -17.2) * mm, "end": v(-5.63, -17.25) * mm});
            skLineSegment(sketch, "E577", {"start": v(-5.65, -17.16) * mm, "end": v(-5.62, -15.61) * mm});
            skArc(sketch, "E578", {"start": v(-5.43, -15.29) * mm, "mid": v(-5.57, -15.42) * mm, "end": v(-5.62, -15.61) * mm});
            skArc(sketch, "E579", {"start": v(-5.1, -15.29) * mm, "mid": v(-5.26, -15.26) * mm, "end": v(-5.43, -15.29) * mm});
            skArc(sketch, "E580", {"start": v(-4.7, -15.68) * mm, "mid": v(-4.87, -15.46) * mm, "end": v(-5.1, -15.29) * mm});
            skLineSegment(sketch, "E581", {"start": v(-4.7, -15.68) * mm, "end": v(-4.63, -13.43) * mm});
            skArc(sketch, "E582", {"start": v(-5.1, -13.9) * mm, "mid": v(-4.82, -13.7) * mm, "end": v(-4.63, -13.43) * mm});
            skArc(sketch, "E583", {"start": v(-5.38, -13.85) * mm, "mid": v(-5.24, -13.9) * mm, "end": v(-5.1, -13.9) * mm});
            skArc(sketch, "E584", {"start": v(-5.52, -13.59) * mm, "mid": v(-5.48, -13.74) * mm, "end": v(-5.38, -13.85) * mm});
            skLineSegment(sketch, "E585", {"start": v(-5.52, -13.59) * mm, "end": v(-5.47, -12.14) * mm});
            skArc(sketch, "E586", {"start": v(-5.28, -11.93) * mm, "mid": v(-5.41, -12) * mm, "end": v(-5.47, -12.14) * mm});
            skLineSegment(sketch, "E587", {"start": v(-5.28, -11.93) * mm, "end": v(-4.56, -11.96) * mm});
            skArc(sketch, "E588", {"start": v(-3.84, -12.55) * mm, "mid": v(-4.1, -12.14) * mm, "end": v(-4.56, -11.96) * mm});
            skLineSegment(sketch, "E589", {"start": v(-3.84, -12.55) * mm, "end": v(-3.78, -10.7) * mm});
            skLineSegment(sketch, "E590", {"start": v(-3.78, -10.7) * mm, "end": v(-7.16, -10.7) * mm});
            skLineSegment(sketch, "E591", {"start": v(-7.16, -10.7) * mm, "end": v(-6.83, -11.14) * mm});
            skLineSegment(sketch, "E592", {"start": v(-1.4, -18.55) * mm, "end": v(-0.87, -18.01) * mm});
            skLineSegment(sketch, "E593", {"start": v(-0.87, -18.01) * mm, "end": v(-0.73, -12.1) * mm});
            skArc(sketch, "E594", {"start": v(-0.73, -12.1) * mm, "mid": v(-0.85, -12) * mm, "end": v(-1, -12) * mm});
            skArc(sketch, "E595", {"start": v(-1, -12) * mm, "mid": v(-1.45, -12.26) * mm, "end": v(-1.67, -12.73) * mm});
            skLineSegment(sketch, "E596", {"start": v(-1.67, -12.73) * mm, "end": v(-1.67, -10.77) * mm});
            skLineSegment(sketch, "E597", {"start": v(-1.67, -10.77) * mm, "end": v(1.74, -10.77) * mm});
            skLineSegment(sketch, "E598", {"start": v(1.74, -10.77) * mm, "end": v(1.74, -12.62) * mm});
            skArc(sketch, "E599", {"start": v(1.74, -12.62) * mm, "mid": v(1.46, -12.22) * mm, "end": v(1.05, -11.95) * mm});
            skArc(sketch, "E600", {"start": v(1.05, -11.95) * mm, "mid": v(0.85, -11.94) * mm, "end": v(0.7, -12.07) * mm});
            skLineSegment(sketch, "E601", {"start": v(0.7, -12.07) * mm, "end": v(0.58, -18.01) * mm});
            skLineSegment(sketch, "E602", {"start": v(0.58, -18.01) * mm, "end": v(0.97, -18.55) * mm});
            skLineSegment(sketch, "E603", {"start": v(0.97, -18.55) * mm, "end": v(-1.4, -18.55) * mm});
            skLineSegment(sketch, "E604", {"start": v(1.55, -18.55) * mm, "end": v(2.1, -18.01) * mm});
            skLineSegment(sketch, "E605", {"start": v(2.1, -18.01) * mm, "end": v(2.23, -11.08) * mm});
            skLineSegment(sketch, "E606", {"start": v(2.23, -11.08) * mm, "end": v(1.89, -10.74) * mm});
            skLineSegment(sketch, "E607", {"start": v(1.89, -10.74) * mm, "end": v(3.96, -10.74) * mm});
            skLineSegment(sketch, "E608", {"start": v(3.96, -10.74) * mm, "end": v(3.69, -11.1) * mm});
            skLineSegment(sketch, "E609", {"start": v(3.69, -11.1) * mm, "end": v(3.58, -13.63) * mm});
            skArc(sketch, "E610", {"start": v(3.58, -13.63) * mm, "mid": v(3.62, -13.77) * mm, "end": v(3.74, -13.87) * mm});
            skLineSegment(sketch, "E611", {"start": v(3.74, -13.87) * mm, "end": v(4.3, -13.87) * mm});
            skArc(sketch, "E612", {"start": v(4.3, -13.87) * mm, "mid": v(4.45, -13.8) * mm, "end": v(4.47, -13.63) * mm});
            skLineSegment(sketch, "E613", {"start": v(4.47, -13.63) * mm, "end": v(4.47, -11.1) * mm});
            skLineSegment(sketch, "E614", {"start": v(4.47, -11.1) * mm, "end": v(4.24, -10.74) * mm});
            skLineSegment(sketch, "E615", {"start": v(4.24, -10.74) * mm, "end": v(6.22, -10.74) * mm});
            skLineSegment(sketch, "E616", {"start": v(6.22, -10.74) * mm, "end": v(5.94, -11.1) * mm});
            skLineSegment(sketch, "E617", {"start": v(5.94, -11.1) * mm, "end": v(5.8, -18.02) * mm});
            skLineSegment(sketch, "E618", {"start": v(5.8, -18.02) * mm, "end": v(6.14, -18.45) * mm});
            skLineSegment(sketch, "E619", {"start": v(6.14, -18.45) * mm, "end": v(4.08, -18.45) * mm});
            skLineSegment(sketch, "E620", {"start": v(4.08, -18.45) * mm, "end": v(4.47, -17.97) * mm});
            skLineSegment(sketch, "E621", {"start": v(4.47, -17.97) * mm, "end": v(4.47, -15.57) * mm});
            skLineSegment(sketch, "E622", {"start": v(4.47, -15.57) * mm, "end": v(4.47, -15.49) * mm});
            skArc(sketch, "E623", {"start": v(4.47, -15.49) * mm, "mid": v(4.4, -15.35) * mm, "end": v(4.26, -15.3) * mm});
            skLineSegment(sketch, "E624", {"start": v(4.26, -15.3) * mm, "end": v(3.77, -15.3) * mm});
            skArc(sketch, "E625", {"start": v(3.77, -15.3) * mm, "mid": v(3.66, -15.35) * mm, "end": v(3.59, -15.45) * mm});
            skLineSegment(sketch, "E626", {"start": v(3.59, -15.45) * mm, "end": v(3.5, -18.01) * mm});
            skLineSegment(sketch, "E627", {"start": v(3.5, -18.01) * mm, "end": v(3.83, -18.48) * mm});
            skLineSegment(sketch, "E628", {"start": v(3.83, -18.48) * mm, "end": v(1.55, -18.55) * mm});
            skLineSegment(sketch, "E629", {"start": v(6.9, -11.07) * mm, "end": v(6.78, -17.88) * mm});
            skLineSegment(sketch, "E630", {"start": v(6.78, -17.88) * mm, "end": v(6.27, -18.45) * mm});
            skLineSegment(sketch, "E631", {"start": v(6.27, -18.45) * mm, "end": v(9.77, -18.45) * mm});
            skLineSegment(sketch, "E632", {"start": v(9.77, -18.45) * mm, "end": v(9.8, -16.73) * mm});
            skLineSegment(sketch, "E633", {"start": v(9.3, -17.2) * mm, "end": v(8.32, -17.2) * mm});
            skArc(sketch, "E634", {"start": v(9.3, -17.2) * mm, "mid": v(9.58, -16.99) * mm, "end": v(9.8, -16.73) * mm});
            skArc(sketch, "E635", {"start": v(8.18, -17.14) * mm, "mid": v(8.25, -17.18) * mm, "end": v(8.32, -17.2) * mm});
            skArc(sketch, "E636", {"start": v(8.16, -17.05) * mm, "mid": v(8.16, -17.1) * mm, "end": v(8.18, -17.14) * mm});
            skLineSegment(sketch, "E637", {"start": v(8.16, -17.05) * mm, "end": v(8.2, -15.5) * mm});
            skArc(sketch, "E638", {"start": v(8.38, -15.18) * mm, "mid": v(8.25, -15.32) * mm, "end": v(8.2, -15.5) * mm});
            skArc(sketch, "E639", {"start": v(8.71, -15.18) * mm, "mid": v(8.55, -15.15) * mm, "end": v(8.38, -15.18) * mm});
            skArc(sketch, "E640", {"start": v(9.11, -15.57) * mm, "mid": v(8.94, -15.35) * mm, "end": v(8.71, -15.18) * mm});
            skLineSegment(sketch, "E641", {"start": v(9.11, -15.57) * mm, "end": v(9.13, -13.42) * mm});
            skArc(sketch, "E642", {"start": v(8.71, -13.79) * mm, "mid": v(8.95, -13.63) * mm, "end": v(9.13, -13.42) * mm});
            skArc(sketch, "E643", {"start": v(8.4, -13.72) * mm, "mid": v(8.55, -13.78) * mm, "end": v(8.71, -13.79) * mm});
            skArc(sketch, "E644", {"start": v(8.24, -13.46) * mm, "mid": v(8.29, -13.61) * mm, "end": v(8.4, -13.72) * mm});
            skLineSegment(sketch, "E645", {"start": v(8.24, -13.46) * mm, "end": v(8.26, -12.04) * mm});
            skArc(sketch, "E646", {"start": v(8.53, -11.82) * mm, "mid": v(8.34, -11.87) * mm, "end": v(8.26, -12.04) * mm});
            skLineSegment(sketch, "E647", {"start": v(8.53, -11.82) * mm, "end": v(9.25, -11.85) * mm});
            skArc(sketch, "E648", {"start": v(9.86, -12.3) * mm, "mid": v(9.62, -11.98) * mm, "end": v(9.25, -11.85) * mm});
            skLineSegment(sketch, "E649", {"start": v(9.86, -12.3) * mm, "end": v(9.9, -10.61) * mm});
            skLineSegment(sketch, "E650", {"start": v(9.9, -10.61) * mm, "end": v(6.5, -10.61) * mm});
            skLineSegment(sketch, "E651", {"start": v(6.5, -10.61) * mm, "end": v(6.9, -11.07) * mm});
            skLineSegment(sketch, "E652", {"start": v(12.02, -15.77) * mm, "end": v(12.1, -17.96) * mm});
            skArc(sketch, "E653", {"start": v(12.1, -17.96) * mm, "mid": v(12.35, -18.21) * mm, "end": v(12.66, -18.37) * mm});
            skArc(sketch, "E654", {"start": v(12.02, -15.77) * mm, "mid": v(12.17, -16.24) * mm, "end": v(12.44, -16.66) * mm});
            skArc(sketch, "E655", {"start": v(12.44, -16.66) * mm, "mid": v(12.83, -16.77) * mm, "end": v(13.22, -16.66) * mm});
            skArc(sketch, "E656", {"start": v(13.22, -16.66) * mm, "mid": v(13.38, -16.46) * mm, "end": v(13.43, -16.21) * mm});
            skArc(sketch, "E657", {"start": v(13.43, -16.21) * mm, "mid": v(13.42, -15.82) * mm, "end": v(13.35, -15.42) * mm});
            skArc(sketch, "E658", {"start": v(13.35, -15.42) * mm, "mid": v(13.3, -15.33) * mm, "end": v(13.25, -15.24) * mm});
            skArc(sketch, "E659", {"start": v(12.1, -14.08) * mm, "mid": v(12.65, -14.68) * mm, "end": v(13.25, -15.24) * mm});
            skLineSegment(sketch, "E660", {"start": v(12.1, -14.08) * mm, "end": v(12.1, -11.34) * mm});
            skArc(sketch, "E661", {"start": v(12.71, -10.63) * mm, "mid": v(12.33, -10.92) * mm, "end": v(12.1, -11.34) * mm});
            skArc(sketch, "E662", {"start": v(13.13, -10.55) * mm, "mid": v(12.91, -10.56) * mm, "end": v(12.71, -10.63) * mm});
            skLineSegment(sketch, "E663", {"start": v(13.13, -10.55) * mm, "end": v(14.3, -10.55) * mm});
            skArc(sketch, "E664", {"start": v(14.83, -11.07) * mm, "mid": v(14.6, -10.77) * mm, "end": v(14.3, -10.55) * mm});
            skLineSegment(sketch, "E665", {"start": v(14.83, -11.07) * mm, "end": v(14.83, -12.82) * mm});
            skArc(sketch, "E666", {"start": v(14.83, -12.82) * mm, "mid": v(14.74, -12.57) * mm, "end": v(14.62, -12.34) * mm});
            skArc(sketch, "E667", {"start": v(14.62, -12.34) * mm, "mid": v(14.47, -12.15) * mm, "end": v(14.27, -12) * mm});
            skArc(sketch, "E668", {"start": v(14.27, -12) * mm, "mid": v(13.95, -11.95) * mm, "end": v(13.64, -12.05) * mm});
            skArc(sketch, "E669", {"start": v(14.72, -14.54) * mm, "mid": v(14.2, -13.9) * mm, "end": v(13.59, -13.34) * mm});
            skLineSegment(sketch, "E670", {"start": v(14.72, -14.54) * mm, "end": v(14.72, -17.63) * mm});
            skArc(sketch, "E671", {"start": v(14.02, -18.37) * mm, "mid": v(14.44, -18.06) * mm, "end": v(14.72, -17.63) * mm});
            skLineSegment(sketch, "E672", {"start": v(12.66, -18.37) * mm, "end": v(14.02, -18.37) * mm});
            skArc(sketch, "E673", {"start": v(13.44, -13.14) * mm, "mid": v(13.5, -13.25) * mm, "end": v(13.59, -13.34) * mm});
            skArc(sketch, "E674", {"start": v(13.44, -12.28) * mm, "mid": v(13.4, -12.7) * mm, "end": v(13.44, -13.14) * mm});
            skArc(sketch, "E675", {"start": v(13.64, -12.05) * mm, "mid": v(13.53, -12.16) * mm, "end": v(13.44, -12.28) * mm});
            skLineSegment(sketch, "E676", {"start": v(15.22, -10.97) * mm, "end": v(15.28, -17.62) * mm});
            skArc(sketch, "E677", {"start": v(15.28, -17.62) * mm, "mid": v(15.56, -18.13) * mm, "end": v(16.04, -18.47) * mm});
            skLineSegment(sketch, "E678", {"start": v(16.04, -18.47) * mm, "end": v(17.7, -18.47) * mm});
            skArc(sketch, "E679", {"start": v(17.7, -18.47) * mm, "mid": v(18.2, -18.13) * mm, "end": v(18.54, -17.62) * mm});
            skLineSegment(sketch, "E680", {"start": v(18.54, -17.62) * mm, "end": v(18.64, -11.07) * mm});
            skLineSegment(sketch, "E681", {"start": v(18.64, -11.07) * mm, "end": v(18.94, -10.62) * mm});
            skLineSegment(sketch, "E682", {"start": v(18.94, -10.62) * mm, "end": v(17.77, -10.62) * mm});
            skArc(sketch, "E683", {"start": v(17.77, -10.62) * mm, "mid": v(17.47, -10.76) * mm, "end": v(17.27, -11.04) * mm});
            skLineSegment(sketch, "E684", {"start": v(15.22, -10.97) * mm, "end": v(14.9, -10.64) * mm});
            skLineSegment(sketch, "E685", {"start": v(14.9, -10.64) * mm, "end": v(16.52, -10.64) * mm});
            skArc(sketch, "E686", {"start": v(16.77, -11.03) * mm, "mid": v(16.7, -10.8) * mm, "end": v(16.52, -10.64) * mm});
            skLineSegment(sketch, "E687", {"start": v(16.77, -11.03) * mm, "end": v(16.68, -16.39) * mm});
            skPoint(sketch, "E688.end.orphan", {"position": v(17.2, -16.39) * mm});
            skLineSegment(sketch, "E689", {"start": v(16.68, -16.39) * mm, "end": v(16.68, -16.6) * mm});
            skArc(sketch, "E690", {"start": v(16.68, -16.6) * mm, "mid": v(16.95, -16.72) * mm, "end": v(17.21, -16.6) * mm});
            skLineSegment(sketch, "E691", {"start": v(17.21, -16.6) * mm, "end": v(17.27, -11.04) * mm});
            skLineSegment(sketch, "E692", {"start": v(19.03, -10.62) * mm, "end": v(19.42, -10.95) * mm});
            skLineSegment(sketch, "E693", {"start": v(19.42, -10.95) * mm, "end": v(19.42, -17.8) * mm});
            skLineSegment(sketch, "E694", {"start": v(19.42, -17.8) * mm, "end": v(18.93, -18.45) * mm});
            skLineSegment(sketch, "E695", {"start": v(18.93, -18.45) * mm, "end": v(20.9, -18.45) * mm});
            skLineSegment(sketch, "E696", {"start": v(20.9, -18.45) * mm, "end": v(20.45, -18.02) * mm});
            skLineSegment(sketch, "E697", {"start": v(20.45, -18.02) * mm, "end": v(20.45, -14.64) * mm});
            skLineSegment(sketch, "E698", {"start": v(20.45, -14.64) * mm, "end": v(21.58, -17.73) * mm});
            skLineSegment(sketch, "E699", {"start": v(21.58, -17.73) * mm, "end": v(21.6, -18.17) * mm});
            skLineSegment(sketch, "E700", {"start": v(21.6, -18.17) * mm, "end": v(21.31, -18.45) * mm});
            skLineSegment(sketch, "E701", {"start": v(21.31, -18.45) * mm, "end": v(23.52, -18.48) * mm});
            skLineSegment(sketch, "E702", {"start": v(23.52, -18.48) * mm, "end": v(23.14, -17.88) * mm});
            skLineSegment(sketch, "E703", {"start": v(23.14, -17.88) * mm, "end": v(23.14, -11.17) * mm});
            skLineSegment(sketch, "E704", {"start": v(23.14, -11.17) * mm, "end": v(23.46, -10.62) * mm});
            skLineSegment(sketch, "E705", {"start": v(23.46, -10.62) * mm, "end": v(21.59, -10.62) * mm});
            skLineSegment(sketch, "E706", {"start": v(21.59, -10.62) * mm, "end": v(21.46, -10.62) * mm});
            skLineSegment(sketch, "E707", {"start": v(21.46, -10.62) * mm, "end": v(21.84, -11.02) * mm});
            skLineSegment(sketch, "E708", {"start": v(21.84, -11.02) * mm, "end": v(21.84, -13.51) * mm});
            skLineSegment(sketch, "E709", {"start": v(21.84, -13.51) * mm, "end": v(20.86, -10.87) * mm});
            skLineSegment(sketch, "E710", {"start": v(20.86, -10.87) * mm, "end": v(20.96, -10.62) * mm});
            skLineSegment(sketch, "E711", {"start": v(20.96, -10.62) * mm, "end": v(19.03, -10.62) * mm});
            skArc(sketch, "E712", {"start": v(-22.08, -14.26) * mm, "mid": v(-21.9, -14.38) * mm, "end": v(-21.73, -14.26) * mm});
            skArc(sketch, "E713", {"start": v(-21.98, -12.3) * mm, "mid": v(-22.07, -13.28) * mm, "end": v(-22.08, -14.26) * mm});
            skArc(sketch, "E714", {"start": v(-21.8, -12.2) * mm, "mid": v(-21.91, -12.22) * mm, "end": v(-21.98, -12.3) * mm});
            skArc(sketch, "E715", {"start": v(-21.69, -12.3) * mm, "mid": v(-21.74, -12.24) * mm, "end": v(-21.8, -12.2) * mm});
            skArc(sketch, "E716", {"start": v(-21.69, -12.3) * mm, "mid": v(-21.72, -13.28) * mm, "end": v(-21.73, -14.26) * mm});
            skArc(sketch, "E717", {"start": v(-18.6, -12.2) * mm, "mid": v(-18.7, -12.97) * mm, "end": v(-18.77, -13.74) * mm});
            skArc(sketch, "E718", {"start": v(-18.45, -12.1) * mm, "mid": v(-18.54, -12.13) * mm, "end": v(-18.6, -12.2) * mm});
            skArc(sketch, "E719", {"start": v(-18.3, -12.2) * mm, "mid": v(-18.37, -12.14) * mm, "end": v(-18.45, -12.1) * mm});
            skArc(sketch, "E720", {"start": v(-18.34, -13.74) * mm, "mid": v(-18.32, -12.97) * mm, "end": v(-18.3, -12.2) * mm});
            skArc(sketch, "E721", {"start": v(-18.77, -13.74) * mm, "mid": v(-18.7, -13.86) * mm, "end": v(-18.58, -13.9) * mm});
            skArc(sketch, "E722", {"start": v(-18.58, -13.9) * mm, "mid": v(-18.43, -13.86) * mm, "end": v(-18.34, -13.74) * mm});
            skArc(sketch, "E723", {"start": v(-15.03, -15.98) * mm, "mid": v(-14.8, -16.08) * mm, "end": v(-14.57, -16) * mm});
            skLineSegment(sketch, "E724", {"start": v(-15.03, -15.98) * mm, "end": v(-14.84, -14.14) * mm});
            skArc(sketch, "E725", {"start": v(-14.77, -14) * mm, "mid": v(-14.82, -14.06) * mm, "end": v(-14.84, -14.14) * mm});
            skArc(sketch, "E726", {"start": v(-14.65, -14) * mm, "mid": v(-14.71, -13.98) * mm, "end": v(-14.77, -14) * mm});
            skArc(sketch, "E727", {"start": v(-14.6, -14.14) * mm, "mid": v(-14.61, -14.07) * mm, "end": v(-14.65, -14) * mm});
            skLineSegment(sketch, "E728", {"start": v(-14.6, -14.14) * mm, "end": v(-14.57, -16) * mm});
            skSolve(sketch);
        }
        {
            var Q0;
            Q0=makeQuery(id+"F4.imprint","IMPRINT",FACE,{"disambiguationData":[TD([[makeQuery(id+"F4.imprint","IMPRINT",EDGE,{"derivedFrom":sQuery(id+"F4.wireOp",EDGE,"E488")}),-1.0]])]});
            var Q1;
            Q1=makeQuery(id+"F4.imprint","IMPRINT",FACE,{"disambiguationData":[TD([[makeQuery(id+"F4.imprint","IMPRINT",EDGE,{"derivedFrom":sQuery(id+"F4.wireOp",EDGE,"E501")}),1.0]])]});
            var Q2;
            Q2=makeQuery(id+"F4.imprint","IMPRINT",FACE,{"disambiguationData":[TD([[makeQuery(id+"F4.imprint","IMPRINT",EDGE,{"derivedFrom":sQuery(id+"F4.wireOp",EDGE,"E517")}),1.0]])]});
            var Q3;
            Q3=makeQuery(id+"F4.imprint","IMPRINT",FACE,{"disambiguationData":[TD([[makeQuery(id+"F4.imprint","IMPRINT",EDGE,{"derivedFrom":sQuery(id+"F4.wireOp",EDGE,"E536")}),1.0]])]});
            var Q4;
            Q4=makeQuery(id+"F4.imprint","IMPRINT",FACE,{"disambiguationData":[TD([[makeQuery(id+"F4.imprint","IMPRINT",EDGE,{"derivedFrom":sQuery(id+"F4.wireOp",EDGE,"E545")}),1.0]])]});
            var Q5;
            Q5=makeQuery(id+"F4.imprint","IMPRINT",FACE,{"disambiguationData":[TD([[makeQuery(id+"F4.imprint","IMPRINT",EDGE,{"derivedFrom":sQuery(id+"F4.wireOp",EDGE,"E569")}),1.0]])]});
            var Q6;
            Q6=makeQuery(id+"F4.imprint","IMPRINT",FACE,{"disambiguationData":[TD([[makeQuery(id+"F4.imprint","IMPRINT",EDGE,{"derivedFrom":sQuery(id+"F4.wireOp",EDGE,"E592")}),-1.0]])]});
            var Q7;
            Q7=makeQuery(id+"F4.imprint","IMPRINT",FACE,{"disambiguationData":[TD([[makeQuery(id+"F4.imprint","IMPRINT",EDGE,{"derivedFrom":sQuery(id+"F4.wireOp",EDGE,"E604")}),-1.0]])]});
            var Q8;
            Q8=makeQuery(id+"F4.imprint","IMPRINT",FACE,{"disambiguationData":[TD([[makeQuery(id+"F4.imprint","IMPRINT",EDGE,{"derivedFrom":sQuery(id+"F4.wireOp",EDGE,"E629")}),1.0]])]});
            var Q9;
            Q9=makeQuery(id+"F4.imprint","IMPRINT",FACE,{"disambiguationData":[TD([[makeQuery(id+"F4.imprint","IMPRINT",EDGE,{"derivedFrom":sQuery(id+"F4.wireOp",EDGE,"E652")}),1.0]])]});
            var Q10;
            Q10=makeQuery(id+"F4.imprint","IMPRINT",FACE,{"disambiguationData":[TD([[makeQuery(id+"F4.imprint","IMPRINT",EDGE,{"derivedFrom":sQuery(id+"F4.wireOp",EDGE,"E676")}),1.0]])]});
            var Q11;
            Q11=makeQuery(id+"F4.imprint","IMPRINT",FACE,{"disambiguationData":[TD([[makeQuery(id+"F4.imprint","IMPRINT",EDGE,{"derivedFrom":sQuery(id+"F4.wireOp",EDGE,"E692")}),1.0]])]});
            extrude(context, id + "F5", {"entities" : qUnion([Q0, Q1, Q2, Q3, Q4, Q5, Q6, Q7, Q8, Q9, Q10, Q11]), "operationType" : NewBodyOperationType.REMOVE, "oppositeDirection" : true, "depth" : .5 * mm});
        }
        {
            var Q0;
            Q0=makeQuery(id+"F1.opExtrude","SWEPT_FACE",FACE,{"disambiguationData":[OSD([sQuery(id+"F0.wireOp",EDGE,"E31")])]});
            var sketch = newSketch(context, id + "F6", { "sketchPlane" : qUnion([Q0])});
            skLineSegment(sketch, "E729.bottom", {"start": v(-25.63, 8) * mm, "end": v(25.27, 8) * mm});
            skLineSegment(sketch, "E729.top", {"start": v(-25.63, 0) * mm, "end": v(25.27, 0) * mm});
            skLineSegment(sketch, "E729.left", {"start": v(-25.63, 8) * mm, "end": v(-25.63, 0) * mm});
            skLineSegment(sketch, "E729.right", {"start": v(25.27, 8) * mm, "end": v(25.27, 0) * mm});
            skLineSegment(sketch, "E730", {"start": v(-25.63, 4) * mm, "end": v(-15.45, 4) * mm, "construction": true});
            skPoint(sketch, "E730.endSnap0", {"position": v(25.27, 4) * mm});
            skLineSegment(sketch, "E731", {"start": v(-15.45, 4) * mm, "end": v(-5.27, 4) * mm, "construction": true});
            skLineSegment(sketch, "E732", {"start": v(-5.27, 4) * mm, "end": v(4.9, 4) * mm, "construction": true});
            skLineSegment(sketch, "E733", {"start": v(4.9, 4) * mm, "end": v(15.09, 4) * mm, "construction": true});
            skLineSegment(sketch, "E734", {"start": v(15.09, 4) * mm, "end": v(25.27, 4) * mm, "construction": true});
            skCircle(sketch, "E735", {"center": v(-20.54, 4) * mm, "radius": 3.5 * mm});
            skCircle(sketch, "E736", {"center": v(-0.18, 4) * mm, "radius": 3.5 * mm});
            skCircle(sketch, "E737", {"center": v(20.18, 4) * mm, "radius": 3.5 * mm});
            skLineSegment(sketch, "E738", {"start": v(-20.54, 4) * mm, "end": v(-20.54, 7.5) * mm, "construction": true});
            skArc(sketch, "E739", {"start": v(-17.04, 4) * mm, "mid": v(-18.07, 6.47) * mm, "end": v(-20.54, 7.5) * mm, "construction": true});
            skLineSegment(sketch, "E740", {"start": v(-20.54, 4) * mm, "end": v(-18.07, 6.47) * mm, "construction": true});
            skLineSegment(sketch, "E741", {"start": v(-18.07, 6.47) * mm, "end": v(-18.07, 1.52) * mm});
            skLineSegment(sketch, "E742", {"start": v(-18.07, 1.52) * mm, "end": v(-23.01, 1.52) * mm});
            skLineSegment(sketch, "E743", {"start": v(-23.01, 1.52) * mm, "end": v(-23.01, 6.47) * mm});
            skLineSegment(sketch, "E744", {"start": v(-23.01, 6.47) * mm, "end": v(-18.07, 6.47) * mm});
            skLineSegment(sketch, "E745", {"start": v(-2.66, 6.47) * mm, "end": v(2.3, 6.47) * mm});
            skLineSegment(sketch, "E746", {"start": v(2.3, 6.47) * mm, "end": v(2.3, 1.53) * mm});
            skLineSegment(sketch, "E747", {"start": v(2.3, 1.53) * mm, "end": v(-2.66, 1.53) * mm});
            skLineSegment(sketch, "E748", {"start": v(-2.66, 1.53) * mm, "end": v(-2.66, 6.47) * mm});
            skLineSegment(sketch, "E749", {"start": v(17.7, 6.47) * mm, "end": v(22.66, 6.47) * mm});
            skLineSegment(sketch, "E750", {"start": v(22.66, 6.47) * mm, "end": v(22.66, 1.53) * mm});
            skLineSegment(sketch, "E751", {"start": v(22.66, 1.53) * mm, "end": v(17.7, 1.53) * mm});
            skLineSegment(sketch, "E752", {"start": v(17.7, 1.53) * mm, "end": v(17.7, 6.47) * mm});
            skPoint(sketch, "E753.orphan", {"position": v(-7.88, 6.47) * mm});
            skPoint(sketch, "E754.end.orphan", {"position": v(-12.84, 6.47) * mm});
            skPoint(sketch, "E755.center.orphan", {"position": v(-10.36, 4) * mm});
            skSolve(sketch);
        }
        {
            var Q0;
            Q0=makeQuery(id+"F6.imprint","IMPRINT",FACE,{"disambiguationData":[TD([[makeQuery(id+"F6.imprint","IMPRINT",EDGE,{"derivedFrom":sQuery(id+"F6.wireOp",EDGE,"E741")}),-1.0]])]});
            var Q1;
            Q1=makeQuery(id+"F6.imprint","IMPRINT",FACE,{"disambiguationData":[TD([[makeQuery(id+"F6.imprint","IMPRINT",EDGE,{"derivedFrom":sQuery(id+"F6.wireOp",EDGE,"C0pnI9zS-IIkk-i9w1-2OOE-Booj0HI0xg05")}),-1.0]])]});
            var Q2;
            Q2=makeQuery(id+"F6.imprint","IMPRINT",FACE,{"disambiguationData":[TD([[makeQuery(id+"F6.imprint","IMPRINT",EDGE,{"derivedFrom":sQuery(id+"F6.wireOp",EDGE,"E745")}),-1.0]])]});
            var Q3;
            Q3=makeQuery(id+"F6.imprint","IMPRINT",FACE,{"disambiguationData":[TD([[makeQuery(id+"F6.imprint","IMPRINT",EDGE,{"derivedFrom":sQuery(id+"F6.wireOp",EDGE,"grYnyDe4-kRcl-tbky-Mbs2-GJaKW8PHMQp2")}),-1.0]])]});
            var Q4;
            Q4=makeQuery(id+"F6.imprint","IMPRINT",FACE,{"disambiguationData":[TD([[makeQuery(id+"F6.imprint","IMPRINT",EDGE,{"derivedFrom":sQuery(id+"F6.wireOp",EDGE,"E749")}),-1.0]])]});
            extrude(context, id + "F7", {"entities" : qUnion([Q0, Q1, Q2, Q3, Q4]), "operationType" : NewBodyOperationType.ADD, "depth" : 5 * mm});
        }
        {
            var Q0;
            Q0=makeQuery(id+"F7.opExtrude","SWEPT_FACE",FACE,{"disambiguationData":[OSD([sQuery(id+"F6.wireOp",EDGE,"E744")])]});
            var sketch = newSketch(context, id + "F8", { "sketchPlane" : qUnion([Q0])});
            skLineSegment(sketch, "E756", {"start": v(-23.01, -25.65) * mm, "end": v(-23.01, -23.15) * mm});
            skLineSegment(sketch, "E757", {"start": v(-23.01, -23.15) * mm, "end": v(-18.07, -23.15) * mm});
            skLineSegment(sketch, "E758", {"start": v(-18.07, -23.15) * mm, "end": v(-18.07, -25.65) * mm});
            skLineSegment(sketch, "E759", {"start": v(-18.07, -25.65) * mm, "end": v(-23.01, -25.65) * mm});
            skSolve(sketch);
        }
        {
            var Q0;
            Q0=makeQuery(id+"F8.imprint","IMPRINT",FACE,{"disambiguationData":[TD([[makeQuery(id+"F8.imprint","IMPRINT",EDGE,{"derivedFrom":sQuery(id+"F8.wireOp",EDGE,"E756")}),-1.0]])]});
            extrude(context, id + "F9", {"entities" : qUnion([Q0]), "operationType" : NewBodyOperationType.ADD, "depth" : 3.5 * mm});
        }
        {
            var Q0;
            Q0=makeQuery(id+"F7.opExtrude","SWEPT_FACE",FACE,{"disambiguationData":[OSD([sQuery(id+"F6.wireOp",EDGE,"E745")])]});
            var sketch = newSketch(context, id + "F10", { "sketchPlane" : qUnion([Q0])});
            skLineSegment(sketch, "E760.bottom", {"start": v(-2.66, -25.65) * mm, "end": v(2.3, -25.65) * mm});
            skLineSegment(sketch, "E760.top", {"start": v(-2.66, -23.15) * mm, "end": v(2.3, -23.15) * mm});
            skLineSegment(sketch, "E760.left", {"start": v(-2.66, -25.65) * mm, "end": v(-2.66, -23.15) * mm});
            skLineSegment(sketch, "E760.right", {"start": v(2.3, -25.65) * mm, "end": v(2.3, -23.15) * mm});
            skSolve(sketch);
        }
        {
            var Q0;
            Q0=makeQuery(id+"F10.imprint","IMPRINT",FACE,{"disambiguationData":[TD([[makeQuery(id+"F10.imprint","IMPRINT",EDGE,{"derivedFrom":sQuery(id+"F10.wireOp",EDGE,"E760.bottom")}),1.0]])]});
            extrude(context, id + "F11", {"entities" : qUnion([Q0]), "operationType" : NewBodyOperationType.ADD, "depth" : 3.5 * mm});
        }
        {
            var Q0;
            Q0=makeQuery(id+"F7.opExtrude","SWEPT_FACE",FACE,{"disambiguationData":[OSD([sQuery(id+"F6.wireOp",EDGE,"E749")])]});
            var sketch = newSketch(context, id + "F12", { "sketchPlane" : qUnion([Q0])});
            skLineSegment(sketch, "E761.bottom", {"start": v(17.7, -25.65) * mm, "end": v(22.66, -25.65) * mm});
            skLineSegment(sketch, "E761.top", {"start": v(17.7, -23.15) * mm, "end": v(22.66, -23.15) * mm});
            skLineSegment(sketch, "E761.left", {"start": v(17.7, -25.65) * mm, "end": v(17.7, -23.15) * mm});
            skLineSegment(sketch, "E761.right", {"start": v(22.66, -25.65) * mm, "end": v(22.66, -23.15) * mm});
            skSolve(sketch);
        }
        {
            var Q0;
            Q0=makeQuery(id+"F12.imprint","IMPRINT",FACE,{"disambiguationData":[TD([[makeQuery(id+"F12.imprint","IMPRINT",EDGE,{"derivedFrom":sQuery(id+"F12.wireOp",EDGE,"E761.bottom")}),1.0]])]});
            extrude(context, id + "F13", {"entities" : qUnion([Q0]), "operationType" : NewBodyOperationType.ADD, "depth" : 3.5 * mm});
        }
        {
            var Q0;
            Q0=makeQuery(id+"F9.boolean.opBoolean","MERGE",FACE,{"derivedFrom":[makeQuery(id+"F7.opExtrude","SWEPT_FACE",FACE,{"disambiguationData":[OSD([sQuery(id+"F6.wireOp",EDGE,"E743")])]}),makeQuery(id+"F9.opExtrude","SWEPT_FACE",FACE,{"disambiguationData":[OSD([sQuery(id+"F8.wireOp",EDGE,"E756")])]})]});
            var sketch = newSketch(context, id + "F14", { "sketchPlane" : qUnion([Q0])});
            skLineSegment(sketch, "E762", {"start": v(6.47, -23.15) * mm, "end": v(6.47, -25.65) * mm, "construction": true});
            skCircle(sketch, "E763", {"center": v(8.22, -23.15) * mm, "radius": 1.25 * mm});
            skSolve(sketch);
        }
        {
            var Q0;
            {var subQ0=sQuery(id+"F14.wireOp",EDGE,"E763");var subQ1=makeQuery(id+"F9.opExtrude","SWEPT_EDGE",EDGE,{"disambiguationData":[OSD([sQuery(id+"F6.wireOp",EDGE,"E743"),sQuery(id+"F6.wireOp",EDGE,"E744"),sQuery(id+"F8.wireOp",EDGE,"E756"),sQuery(id+"F8.wireOp",EDGE,"E757")])]});var subQ2=makeQuery(id+"F14.imprint","INTERSECT",VERTEX,{"disambiguationData":[OD(0.0)],"derivedFrom":[subQ1,subQ0]});Q0=makeQuery(id+"F14.imprint","IMPRINT",FACE,{"disambiguationData":[TD([[makeQuery(id+"F14.imprint","IMPRINT",EDGE,{"disambiguationData":[TD([[subQ2,-1.0]])],"derivedFrom":subQ0}),1.0]])]});}
            var Q1;
            {var subQ0=sQuery(id+"F14.wireOp",EDGE,"E763");var subQ1=makeQuery(id+"F9.opExtrude","SWEPT_EDGE",EDGE,{"disambiguationData":[OSD([sQuery(id+"F6.wireOp",EDGE,"E743"),sQuery(id+"F6.wireOp",EDGE,"E744"),sQuery(id+"F8.wireOp",EDGE,"E756"),sQuery(id+"F8.wireOp",EDGE,"E757")])]});var subQ2=makeQuery(id+"F14.imprint","INTERSECT",VERTEX,{"disambiguationData":[OD(0.0)],"derivedFrom":[subQ1,subQ0]});Q1=makeQuery(id+"F14.imprint","IMPRINT",FACE,{"disambiguationData":[TD([[makeQuery(id+"F14.imprint","IMPRINT",EDGE,{"disambiguationData":[TD([[subQ2,1.0]])],"derivedFrom":subQ0}),1.0]])]});}
            extrude(context, id + "F15", {"entities" : qUnion([Q0, Q1]), "operationType" : NewBodyOperationType.REMOVE, "oppositeDirection" : true, "depth" : 50 * mm});
        }
        {
            var Q0;
            Q0=makeQuery(id+"F15.boolean.opBoolean","INTERSECT",EDGE,{"disambiguationData":[OD(1.0)],"derivedFrom":[makeQuery(id+"F9.opExtrude","SWEPT_FACE",FACE,{"disambiguationData":[OSD([sQuery(id+"F8.wireOp",EDGE,"E757")])]}),makeQuery(id+"F15.opExtrude","SWEPT_FACE",FACE,{"disambiguationData":[OSD([sQuery(id+"F14.wireOp",EDGE,"E763")])]})]});
            var Q1;
            Q1=makeQuery(id+"F15.boolean.opBoolean","INTERSECT",EDGE,{"disambiguationData":[OD(1.0)],"derivedFrom":[makeQuery(id+"FsrXEuAfvPgkNLM_11.opExtrude","SWEPT_FACE",FACE,{"disambiguationData":[OSD([sQuery(id+"FNCmPUbI0wSzkhS_11.wireOp",EDGE,"ZP21JJqy-wLOn-HU24-3H5G-HBB2CVayaNa2.top")])]}),makeQuery(id+"F15.opExtrude","SWEPT_FACE",FACE,{"disambiguationData":[OSD([sQuery(id+"F14.wireOp",EDGE,"E763")])]})]});
            var Q2;
            Q2=makeQuery(id+"F15.boolean.opBoolean","INTERSECT",EDGE,{"disambiguationData":[OD(1.0)],"derivedFrom":[makeQuery(id+"F11.opExtrude","SWEPT_FACE",FACE,{"disambiguationData":[OSD([sQuery(id+"F10.wireOp",EDGE,"E760.top")])]}),makeQuery(id+"F15.opExtrude","SWEPT_FACE",FACE,{"disambiguationData":[OSD([sQuery(id+"F14.wireOp",EDGE,"E763")])]})]});
            var Q3;
            Q3=makeQuery(id+"F15.boolean.opBoolean","INTERSECT",EDGE,{"disambiguationData":[OD(1.0)],"derivedFrom":[makeQuery(id+"F3hXsfmJ9TlrLTD_11.opExtrude","SWEPT_FACE",FACE,{"disambiguationData":[OSD([sQuery(id+"FnjNTP1BDCPo5km_11.wireOp",EDGE,"JkY4gohi-YhOk-WpzL-dtk2-bwTpimeT2VBO.top")])]}),makeQuery(id+"F15.opExtrude","SWEPT_FACE",FACE,{"disambiguationData":[OSD([sQuery(id+"F14.wireOp",EDGE,"E763")])]})]});
            var Q4;
            Q4=makeQuery(id+"F15.boolean.opBoolean","INTERSECT",EDGE,{"disambiguationData":[OD(1.0)],"derivedFrom":[makeQuery(id+"F13.opExtrude","SWEPT_FACE",FACE,{"disambiguationData":[OSD([sQuery(id+"F12.wireOp",EDGE,"E761.top")])]}),makeQuery(id+"F15.opExtrude","SWEPT_FACE",FACE,{"disambiguationData":[OSD([sQuery(id+"F14.wireOp",EDGE,"E763")])]})]});
            fillet(context, id + "F16", {"entities" : qUnion([Q0, Q1, Q2, Q3, Q4]), "radius" : .75 * mm, "tangentPropagation" : true, "allowEdgeOverflow" : false});
        }
        {
            var Q0;
            Q0=makeQuery(id+"F15.boolean.opBoolean","INTERSECT",EDGE,{"disambiguationData":[OD(0.0)],"derivedFrom":[makeQuery(id+"F9.opExtrude","SWEPT_FACE",FACE,{"disambiguationData":[OSD([sQuery(id+"F8.wireOp",EDGE,"E757")])]}),makeQuery(id+"F15.opExtrude","SWEPT_FACE",FACE,{"disambiguationData":[OSD([sQuery(id+"F14.wireOp",EDGE,"E763")])]})]});
            var Q1;
            Q1=makeQuery(id+"F9.opExtrude","CAP_EDGE",EDGE,{"disambiguationData":[OSD([sQuery(id+"F8.wireOp",EDGE,"E757")])],"isStart":false});
            var Q2;
            Q2=makeQuery(id+"F15.boolean.opBoolean","INTERSECT",EDGE,{"disambiguationData":[OD(0.0)],"derivedFrom":[makeQuery(id+"FsrXEuAfvPgkNLM_11.opExtrude","SWEPT_FACE",FACE,{"disambiguationData":[OSD([sQuery(id+"FNCmPUbI0wSzkhS_11.wireOp",EDGE,"ZP21JJqy-wLOn-HU24-3H5G-HBB2CVayaNa2.top")])]}),makeQuery(id+"F15.opExtrude","SWEPT_FACE",FACE,{"disambiguationData":[OSD([sQuery(id+"F14.wireOp",EDGE,"E763")])]})]});
            var Q3;
            Q3=makeQuery(id+"FsrXEuAfvPgkNLM_11.opExtrude","CAP_EDGE",EDGE,{"disambiguationData":[OSD([sQuery(id+"FNCmPUbI0wSzkhS_11.wireOp",EDGE,"ZP21JJqy-wLOn-HU24-3H5G-HBB2CVayaNa2.top")])],"isStart":false});
            var Q4;
            Q4=makeQuery(id+"F15.boolean.opBoolean","INTERSECT",EDGE,{"disambiguationData":[OD(0.0)],"derivedFrom":[makeQuery(id+"F11.opExtrude","SWEPT_FACE",FACE,{"disambiguationData":[OSD([sQuery(id+"F10.wireOp",EDGE,"E760.top")])]}),makeQuery(id+"F15.opExtrude","SWEPT_FACE",FACE,{"disambiguationData":[OSD([sQuery(id+"F14.wireOp",EDGE,"E763")])]})]});
            var Q5;
            Q5=makeQuery(id+"F11.opExtrude","CAP_EDGE",EDGE,{"disambiguationData":[OSD([sQuery(id+"F10.wireOp",EDGE,"E760.top")])],"isStart":false});
            var Q6;
            Q6=makeQuery(id+"F15.boolean.opBoolean","INTERSECT",EDGE,{"disambiguationData":[OD(0.0)],"derivedFrom":[makeQuery(id+"F3hXsfmJ9TlrLTD_11.opExtrude","SWEPT_FACE",FACE,{"disambiguationData":[OSD([sQuery(id+"FnjNTP1BDCPo5km_11.wireOp",EDGE,"JkY4gohi-YhOk-WpzL-dtk2-bwTpimeT2VBO.top")])]}),makeQuery(id+"F15.opExtrude","SWEPT_FACE",FACE,{"disambiguationData":[OSD([sQuery(id+"F14.wireOp",EDGE,"E763")])]})]});
            var Q7;
            Q7=makeQuery(id+"F3hXsfmJ9TlrLTD_11.opExtrude","CAP_EDGE",EDGE,{"disambiguationData":[OSD([sQuery(id+"FnjNTP1BDCPo5km_11.wireOp",EDGE,"JkY4gohi-YhOk-WpzL-dtk2-bwTpimeT2VBO.top")])],"isStart":false});
            var Q8;
            Q8=makeQuery(id+"F15.boolean.opBoolean","INTERSECT",EDGE,{"disambiguationData":[OD(0.0)],"derivedFrom":[makeQuery(id+"F13.opExtrude","SWEPT_FACE",FACE,{"disambiguationData":[OSD([sQuery(id+"F12.wireOp",EDGE,"E761.top")])]}),makeQuery(id+"F15.opExtrude","SWEPT_FACE",FACE,{"disambiguationData":[OSD([sQuery(id+"F14.wireOp",EDGE,"E763")])]})]});
            var Q9;
            Q9=makeQuery(id+"F13.opExtrude","CAP_EDGE",EDGE,{"disambiguationData":[OSD([sQuery(id+"F12.wireOp",EDGE,"E761.top")])],"isStart":false});
            fillet(context, id + "F17", {"entities" : qUnion([Q0, Q1, Q2, Q3, Q4, Q5, Q6, Q7, Q8, Q9]), "radius" : .15 * mm, "tangentPropagation" : true, "allowEdgeOverflow" : false});
        }
        {
            var Q0;
            Q0=makeQuery(id+"F11.opExtrude","CAP_EDGE",EDGE,{"disambiguationData":[OSD([sQuery(id+"F10.wireOp",EDGE,"E760.left")])],"isStart":false});
            var Q1;
            Q1=makeQuery(id+"F11.opExtrude","CAP_EDGE",EDGE,{"disambiguationData":[OSD([sQuery(id+"F10.wireOp",EDGE,"E760.bottom")])],"isStart":false});
            var Q2;
            Q2=makeQuery(id+"F11.boolean.opBoolean","MERGE",EDGE,{"derivedFrom":[makeQuery(id+"F7.opExtrude","CAP_EDGE",EDGE,{"disambiguationData":[OSD([sQuery(id+"F6.wireOp",EDGE,"E748")])],"isStart":false}),makeQuery(id+"F11.opExtrude","SWEPT_EDGE",EDGE,{"disambiguationData":[OSD([sQuery(id+"F10.wireOp",EDGE,"E760.bottom"),sQuery(id+"F10.wireOp",EDGE,"E760.left")])]})]});
            var Q3;
            Q3=makeQuery(id+"FsrXEuAfvPgkNLM_11.boolean.opBoolean","MERGE",EDGE,{"derivedFrom":[makeQuery(id+"F7.opExtrude","CAP_EDGE",EDGE,{"disambiguationData":[OSD([sQuery(id+"F6.wireOp",EDGE,"E754")])],"isStart":false}),makeQuery(id+"FsrXEuAfvPgkNLM_11.opExtrude","SWEPT_EDGE",EDGE,{"disambiguationData":[OSD([sQuery(id+"FNCmPUbI0wSzkhS_11.wireOp",EDGE,"ZP21JJqy-wLOn-HU24-3H5G-HBB2CVayaNa2.bottom"),sQuery(id+"FNCmPUbI0wSzkhS_11.wireOp",EDGE,"ZP21JJqy-wLOn-HU24-3H5G-HBB2CVayaNa2.left")])]})]});
            var Q4;
            Q4=makeQuery(id+"FsrXEuAfvPgkNLM_11.opExtrude","CAP_EDGE",EDGE,{"disambiguationData":[OSD([sQuery(id+"FNCmPUbI0wSzkhS_11.wireOp",EDGE,"ZP21JJqy-wLOn-HU24-3H5G-HBB2CVayaNa2.bottom")])],"isStart":false});
            var Q5;
            Q5=makeQuery(id+"FsrXEuAfvPgkNLM_11.opExtrude","CAP_EDGE",EDGE,{"disambiguationData":[OSD([sQuery(id+"FNCmPUbI0wSzkhS_11.wireOp",EDGE,"ZP21JJqy-wLOn-HU24-3H5G-HBB2CVayaNa2.left")])],"isStart":false});
            var Q6;
            Q6=makeQuery(id+"F9.boolean.opBoolean","MERGE",EDGE,{"derivedFrom":[makeQuery(id+"F7.opExtrude","CAP_EDGE",EDGE,{"disambiguationData":[OSD([sQuery(id+"F6.wireOp",EDGE,"E743")])],"isStart":false}),makeQuery(id+"F9.opExtrude","SWEPT_EDGE",EDGE,{"disambiguationData":[OSD([sQuery(id+"F8.wireOp",EDGE,"E756"),sQuery(id+"F8.wireOp",EDGE,"E759")])]})]});
            var Q7;
            Q7=makeQuery(id+"F9.opExtrude","CAP_EDGE",EDGE,{"disambiguationData":[OSD([sQuery(id+"F8.wireOp",EDGE,"E756")])],"isStart":false});
            var Q8;
            Q8=makeQuery(id+"F9.opExtrude","CAP_EDGE",EDGE,{"disambiguationData":[OSD([sQuery(id+"F8.wireOp",EDGE,"E759")])],"isStart":false});
            var Q9;
            Q9=makeQuery(id+"F3hXsfmJ9TlrLTD_11.opExtrude","CAP_EDGE",EDGE,{"disambiguationData":[OSD([sQuery(id+"FnjNTP1BDCPo5km_11.wireOp",EDGE,"JkY4gohi-YhOk-WpzL-dtk2-bwTpimeT2VBO.left")])],"isStart":false});
            var Q10;
            Q10=makeQuery(id+"F3hXsfmJ9TlrLTD_11.boolean.opBoolean","MERGE",EDGE,{"derivedFrom":[makeQuery(id+"F7.opExtrude","CAP_EDGE",EDGE,{"disambiguationData":[OSD([sQuery(id+"F6.wireOp",EDGE,"soOEqwbj-cfrq-9okC-bMRW-coRcyFQHYqih")])],"isStart":false}),makeQuery(id+"F3hXsfmJ9TlrLTD_11.opExtrude","SWEPT_EDGE",EDGE,{"disambiguationData":[OSD([sQuery(id+"FnjNTP1BDCPo5km_11.wireOp",EDGE,"JkY4gohi-YhOk-WpzL-dtk2-bwTpimeT2VBO.bottom"),sQuery(id+"FnjNTP1BDCPo5km_11.wireOp",EDGE,"JkY4gohi-YhOk-WpzL-dtk2-bwTpimeT2VBO.left")])]})]});
            var Q11;
            Q11=makeQuery(id+"F3hXsfmJ9TlrLTD_11.opExtrude","CAP_EDGE",EDGE,{"disambiguationData":[OSD([sQuery(id+"FnjNTP1BDCPo5km_11.wireOp",EDGE,"JkY4gohi-YhOk-WpzL-dtk2-bwTpimeT2VBO.bottom")])],"isStart":false});
            var Q12;
            Q12=makeQuery(id+"F13.opExtrude","CAP_EDGE",EDGE,{"disambiguationData":[OSD([sQuery(id+"F12.wireOp",EDGE,"E761.left")])],"isStart":false});
            var Q13;
            Q13=makeQuery(id+"F13.boolean.opBoolean","MERGE",EDGE,{"derivedFrom":[makeQuery(id+"F7.opExtrude","CAP_EDGE",EDGE,{"disambiguationData":[OSD([sQuery(id+"F6.wireOp",EDGE,"E752")])],"isStart":false}),makeQuery(id+"F13.opExtrude","SWEPT_EDGE",EDGE,{"disambiguationData":[OSD([sQuery(id+"F12.wireOp",EDGE,"E761.bottom"),sQuery(id+"F12.wireOp",EDGE,"E761.left")])]})]});
            var Q14;
            Q14=makeQuery(id+"F13.opExtrude","CAP_EDGE",EDGE,{"disambiguationData":[OSD([sQuery(id+"F12.wireOp",EDGE,"E761.bottom")])],"isStart":false});
            var Q15;
            Q15=makeQuery(id+"F13.opExtrude","CAP_EDGE",EDGE,{"disambiguationData":[OSD([sQuery(id+"F12.wireOp",EDGE,"E761.right")])],"isStart":false});
            var Q16;
            Q16=makeQuery(id+"F13.boolean.opBoolean","MERGE",EDGE,{"derivedFrom":[makeQuery(id+"F7.opExtrude","CAP_EDGE",EDGE,{"disambiguationData":[OSD([sQuery(id+"F6.wireOp",EDGE,"E750")])],"isStart":false}),makeQuery(id+"F13.opExtrude","SWEPT_EDGE",EDGE,{"disambiguationData":[OSD([sQuery(id+"F12.wireOp",EDGE,"E761.bottom"),sQuery(id+"F12.wireOp",EDGE,"E761.right")])]})]});
            var Q17;
            Q17=makeQuery(id+"F3hXsfmJ9TlrLTD_11.opExtrude","CAP_EDGE",EDGE,{"disambiguationData":[OSD([sQuery(id+"FnjNTP1BDCPo5km_11.wireOp",EDGE,"JkY4gohi-YhOk-WpzL-dtk2-bwTpimeT2VBO.right")])],"isStart":false});
            var Q18;
            Q18=makeQuery(id+"F3hXsfmJ9TlrLTD_11.boolean.opBoolean","MERGE",EDGE,{"derivedFrom":[makeQuery(id+"F7.opExtrude","CAP_EDGE",EDGE,{"disambiguationData":[OSD([sQuery(id+"F6.wireOp",EDGE,"aB7oslHW-Hx75-BNz2-Om8Q-vojMFV6Zoena")])],"isStart":false}),makeQuery(id+"F3hXsfmJ9TlrLTD_11.opExtrude","SWEPT_EDGE",EDGE,{"disambiguationData":[OSD([sQuery(id+"FnjNTP1BDCPo5km_11.wireOp",EDGE,"JkY4gohi-YhOk-WpzL-dtk2-bwTpimeT2VBO.bottom"),sQuery(id+"FnjNTP1BDCPo5km_11.wireOp",EDGE,"JkY4gohi-YhOk-WpzL-dtk2-bwTpimeT2VBO.right")])]})]});
            var Q19;
            Q19=makeQuery(id+"F11.opExtrude","CAP_EDGE",EDGE,{"disambiguationData":[OSD([sQuery(id+"F10.wireOp",EDGE,"E760.right")])],"isStart":false});
            var Q20;
            Q20=makeQuery(id+"F11.boolean.opBoolean","MERGE",EDGE,{"derivedFrom":[makeQuery(id+"F7.opExtrude","CAP_EDGE",EDGE,{"disambiguationData":[OSD([sQuery(id+"F6.wireOp",EDGE,"E746")])],"isStart":false}),makeQuery(id+"F11.opExtrude","SWEPT_EDGE",EDGE,{"disambiguationData":[OSD([sQuery(id+"F10.wireOp",EDGE,"E760.bottom"),sQuery(id+"F10.wireOp",EDGE,"E760.right")])]})]});
            var Q21;
            Q21=makeQuery(id+"FsrXEuAfvPgkNLM_11.opExtrude","CAP_EDGE",EDGE,{"disambiguationData":[OSD([sQuery(id+"FNCmPUbI0wSzkhS_11.wireOp",EDGE,"ZP21JJqy-wLOn-HU24-3H5G-HBB2CVayaNa2.right")])],"isStart":false});
            var Q22;
            Q22=makeQuery(id+"FsrXEuAfvPgkNLM_11.boolean.opBoolean","MERGE",EDGE,{"derivedFrom":[makeQuery(id+"F7.opExtrude","CAP_EDGE",EDGE,{"disambiguationData":[OSD([sQuery(id+"F6.wireOp",EDGE,"ROlelOZJ-AS3Q-hMtw-PtDJ-Mo5dy9f0Fgtu")])],"isStart":false}),makeQuery(id+"FsrXEuAfvPgkNLM_11.opExtrude","SWEPT_EDGE",EDGE,{"disambiguationData":[OSD([sQuery(id+"FNCmPUbI0wSzkhS_11.wireOp",EDGE,"ZP21JJqy-wLOn-HU24-3H5G-HBB2CVayaNa2.bottom"),sQuery(id+"FNCmPUbI0wSzkhS_11.wireOp",EDGE,"ZP21JJqy-wLOn-HU24-3H5G-HBB2CVayaNa2.right")])]})]});
            var Q23;
            Q23=makeQuery(id+"F9.opExtrude","CAP_EDGE",EDGE,{"disambiguationData":[OSD([sQuery(id+"F8.wireOp",EDGE,"E758")])],"isStart":false});
            var Q24;
            Q24=makeQuery(id+"F9.boolean.opBoolean","MERGE",EDGE,{"derivedFrom":[makeQuery(id+"F7.opExtrude","CAP_EDGE",EDGE,{"disambiguationData":[OSD([sQuery(id+"F6.wireOp",EDGE,"E741")])],"isStart":false}),makeQuery(id+"F9.opExtrude","SWEPT_EDGE",EDGE,{"disambiguationData":[OSD([sQuery(id+"F8.wireOp",EDGE,"E758"),sQuery(id+"F8.wireOp",EDGE,"E759")])]})]});
            fillet(context, id + "F18", {"entities" : qUnion([Q0, Q1, Q2, Q3, Q4, Q5, Q6, Q7, Q8, Q9, Q10, Q11, Q12, Q13, Q14, Q15, Q16, Q17, Q18, Q19, Q20, Q21, Q22, Q23, Q24]), "radius" : .15 * mm, "tangentPropagation" : true, "allowEdgeOverflow" : false});
        }
        {
            var Q0;
            Q0=makeQuery(id+"F1.opExtrude","CAP_EDGE",EDGE,{"disambiguationData":[OSD([sQuery(id+"F0.wireOp",EDGE,"E26"),sQuery(id+"F0.wireOp",EDGE,"E29")])],"isStart":false});
            var Q1;
            Q1=makeQuery(id+"F1.opExtrude","CAP_EDGE",EDGE,{"disambiguationData":[OSD([sQuery(id+"F0.wireOp",EDGE,"E28"),sQuery(id+"F0.wireOp",EDGE,"E235")])],"isStart":false});
            var Q2;
            Q2=makeQuery(id+"F1.opExtrude","CAP_EDGE",EDGE,{"disambiguationData":[OSD([sQuery(id+"F0.wireOp",EDGE,"E28"),sQuery(id+"F0.wireOp",EDGE,"E235")])],"isStart":true});
            var Q3;
            Q3=makeQuery(id+"F1.opExtrude","SWEPT_EDGE",EDGE,{"disambiguationData":[OSD([sQuery(id+"F0.wireOp",EDGE,"E28"),sQuery(id+"F0.wireOp",EDGE,"E29")])]});
            var Q4;
            Q4=makeQuery(id+"F1.opExtrude","CAP_EDGE",EDGE,{"disambiguationData":[OSD([sQuery(id+"F0.wireOp",EDGE,"E26"),sQuery(id+"F0.wireOp",EDGE,"E29")])],"isStart":true});
            var Q5;
            Q5=makeQuery(id+"F1.opExtrude","CAP_EDGE",EDGE,{"disambiguationData":[OSD([sQuery(id+"F0.wireOp",EDGE,"E33")])],"isStart":false});
            var Q6;
            Q6=makeQuery(id+"F1.opExtrude","CAP_EDGE",EDGE,{"disambiguationData":[OSD([sQuery(id+"F0.wireOp",EDGE,"E33")])],"isStart":true});
            var Q7;
            Q7=makeQuery(id+"F1.opExtrude","SWEPT_EDGE",EDGE,{"disambiguationData":[OSD([sQuery(id+"F0.wireOp",EDGE,"E33"),sQuery(id+"F0.wireOp",EDGE,"E34")])]});
            var Q8;
            Q8=makeQuery(id+"F1.opExtrude","CAP_EDGE",EDGE,{"disambiguationData":[OSD([sQuery(id+"F0.wireOp",EDGE,"E34")])],"isStart":false});
            var Q9;
            Q9=makeQuery(id+"F1.opExtrude","CAP_EDGE",EDGE,{"disambiguationData":[OSD([sQuery(id+"F0.wireOp",EDGE,"E234")])],"isStart":false});
            var Q10;
            Q10=makeQuery(id+"F1.opExtrude","SWEPT_EDGE",EDGE,{"disambiguationData":[OSD([sQuery(id+"F0.wireOp",EDGE,"E31"),sQuery(id+"F0.wireOp",EDGE,"E235")])]});
            var Q11;
            Q11=makeQuery(id+"F1.opExtrude","CAP_EDGE",EDGE,{"disambiguationData":[OSD([sQuery(id+"F0.wireOp",EDGE,"E31")])],"isStart":false});
            var Q12;
            Q12=makeQuery(id+"F1.opExtrude","SWEPT_EDGE",EDGE,{"disambiguationData":[OSD([sQuery(id+"F0.wireOp",EDGE,"E31"),sQuery(id+"F0.wireOp",EDGE,"E234")])]});
            var Q13;
            Q13=makeQuery(id+"F1.opExtrude","CAP_EDGE",EDGE,{"disambiguationData":[OSD([sQuery(id+"F0.wireOp",EDGE,"E34")])],"isStart":true});
            var Q14;
            Q14=makeQuery(id+"F1.opExtrude","CAP_EDGE",EDGE,{"disambiguationData":[OSD([sQuery(id+"F0.wireOp",EDGE,"E234")])],"isStart":true});
            var Q15;
            Q15=makeQuery(id+"F1.opExtrude","CAP_EDGE",EDGE,{"disambiguationData":[OSD([sQuery(id+"F0.wireOp",EDGE,"E31")])],"isStart":true});
            fillet(context, id + "F19", {"entities" : qUnion([Q0, Q1, Q2, Q3, Q4, Q5, Q6, Q7, Q8, Q9, Q10, Q11, Q12, Q13, Q14, Q15]), "radius" : .15 * mm, "tangentPropagation" : true, "allowEdgeOverflow" : false});
        }
    });
